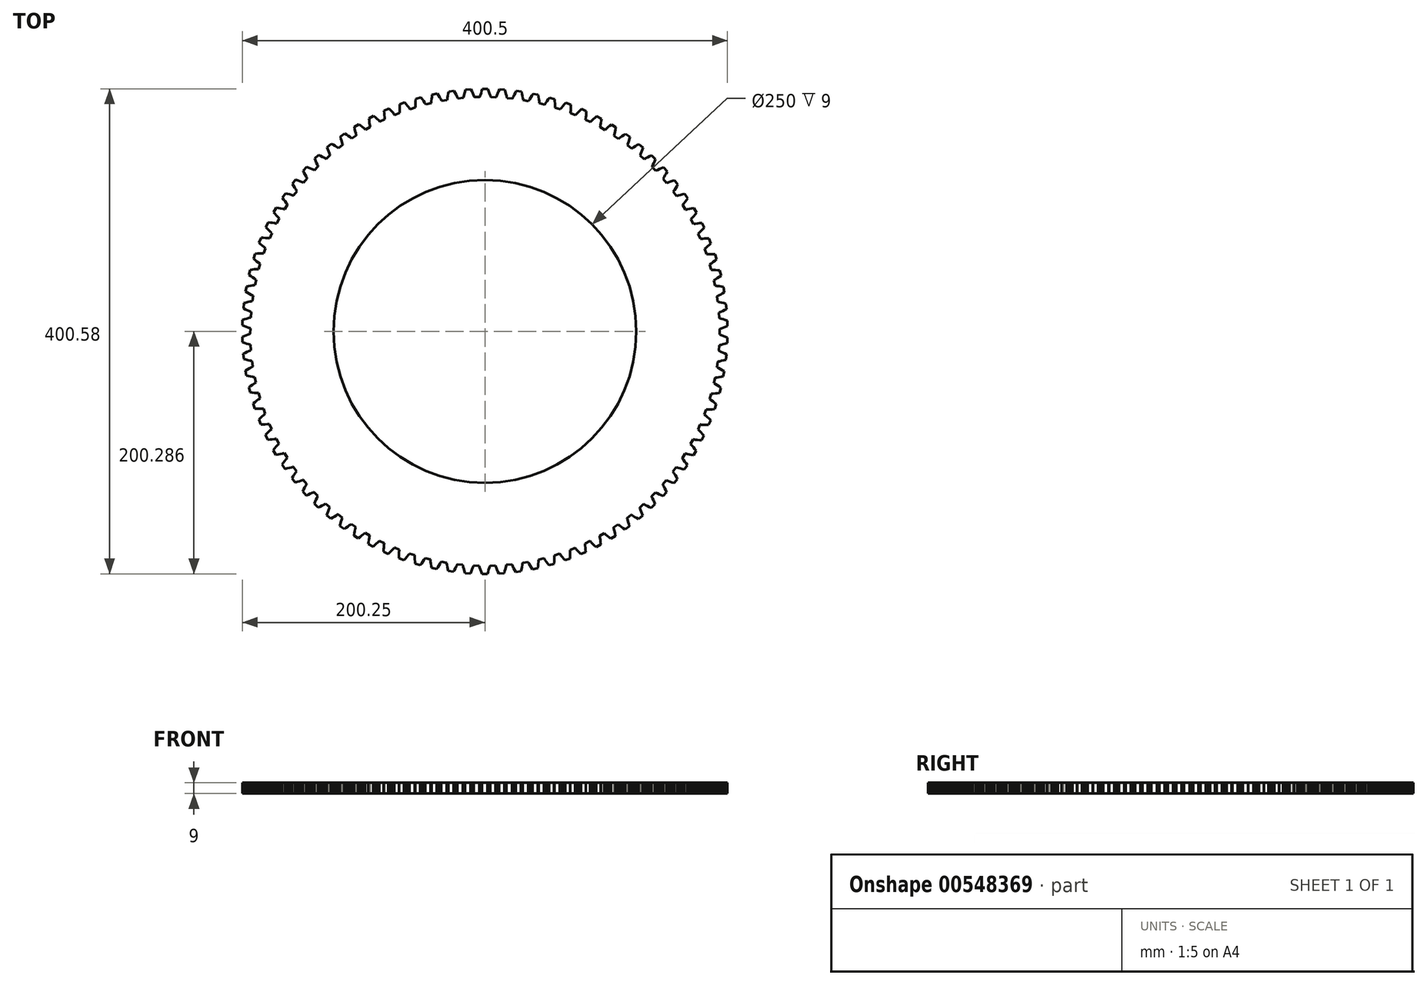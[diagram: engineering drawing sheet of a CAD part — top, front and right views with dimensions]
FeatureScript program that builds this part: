
annotation { "Feature Type Name" : "Feature", "Feature Type Description" : "" }
export const myFeature = defineFeature(function(context is Context, id is Id, definition is map)
    precondition{}
    {
        {
            var Q0;
            Q0=qCreatedBy(makeId("Top.planeOp"),FACE);
            var sketch = newSketch(context, id + "F0", { "sketchPlane" : qUnion([Q0])});
            skLineSegment(sketch, "E0.0.0", {"start": v(83.63, 88.8) * mm, "end": v(83.62, 84.25) * mm});
            skLineSegment(sketch, "E0.0.1", {"start": v(83.62, 84.25) * mm, "end": v(84.03, 84.11) * mm});
            skLineSegment(sketch, "E0.0.2", {"start": v(84.03, 84.11) * mm, "end": v(84.44, 83.97) * mm});
            skLineSegment(sketch, "E0.0.3", {"start": v(84.44, 83.97) * mm, "end": v(85.27, 83.69) * mm});
            skLineSegment(sketch, "E0.0.4", {"start": v(85.27, 83.69) * mm, "end": v(86.9, 83.08) * mm});
            skLineSegment(sketch, "E0.0.5", {"start": v(86.9, 83.08) * mm, "end": v(88.54, 82.43) * mm});
            skLineSegment(sketch, "E0.0.6", {"start": v(88.54, 82.43) * mm, "end": v(90.18, 81.73) * mm});
            skLineSegment(sketch, "E0.0.7", {"start": v(90.18, 81.73) * mm, "end": v(90.02, 77.33) * mm});
            skLineSegment(sketch, "E0.0.8", {"start": v(90.02, 77.33) * mm, "end": v(88.34, 76.75) * mm});
            skLineSegment(sketch, "E0.0.9", {"start": v(88.34, 76.75) * mm, "end": v(86.66, 76.21) * mm});
            skLineSegment(sketch, "E0.0.10", {"start": v(86.66, 76.21) * mm, "end": v(84.98, 75.72) * mm});
            skLineSegment(sketch, "E0.0.11", {"start": v(84.98, 75.72) * mm, "end": v(84.14, 75.5) * mm});
            skLineSegment(sketch, "E0.0.12", {"start": v(84.14, 75.5) * mm, "end": v(83.72, 75.4) * mm});
            skLineSegment(sketch, "E0.0.13", {"start": v(83.72, 75.4) * mm, "end": v(83.3, 75.29) * mm});
            skLineSegment(sketch, "E0.0.14", {"start": v(83.3, 75.29) * mm, "end": v(82.97, 70.74) * mm});
            skLineSegment(sketch, "E0.0.15", {"start": v(82.97, 70.74) * mm, "end": v(83.37, 70.58) * mm});
            skLineSegment(sketch, "E0.0.16", {"start": v(83.37, 70.58) * mm, "end": v(83.77, 70.41) * mm});
            skLineSegment(sketch, "E0.0.17", {"start": v(83.77, 70.41) * mm, "end": v(84.57, 70.07) * mm});
            skLineSegment(sketch, "E0.0.18", {"start": v(84.57, 70.07) * mm, "end": v(86.17, 69.35) * mm});
            skLineSegment(sketch, "E0.0.19", {"start": v(86.17, 69.35) * mm, "end": v(87.75, 68.58) * mm});
            skLineSegment(sketch, "E0.0.20", {"start": v(87.75, 68.58) * mm, "end": v(89.33, 67.77) * mm});
            skLineSegment(sketch, "E0.0.21", {"start": v(89.33, 67.77) * mm, "end": v(88.87, 63.4) * mm});
            skLineSegment(sketch, "E0.0.22", {"start": v(88.87, 63.4) * mm, "end": v(87.15, 62.93) * mm});
            skLineSegment(sketch, "E0.0.23", {"start": v(87.15, 62.93) * mm, "end": v(85.44, 62.51) * mm});
            skLineSegment(sketch, "E0.0.24", {"start": v(85.44, 62.51) * mm, "end": v(83.73, 62.15) * mm});
            skLineSegment(sketch, "E0.0.25", {"start": v(83.73, 62.15) * mm, "end": v(82.88, 61.98) * mm});
            skLineSegment(sketch, "E0.0.26", {"start": v(82.88, 61.98) * mm, "end": v(82.45, 61.9) * mm});
            skLineSegment(sketch, "E0.0.27", {"start": v(82.45, 61.9) * mm, "end": v(82.02, 61.83) * mm});
            skLineSegment(sketch, "E0.0.28", {"start": v(82.02, 61.83) * mm, "end": v(81.38, 57.31) * mm});
            skLineSegment(sketch, "E0.0.29", {"start": v(81.38, 57.31) * mm, "end": v(81.77, 57.12) * mm});
            skLineSegment(sketch, "E0.0.30", {"start": v(81.77, 57.12) * mm, "end": v(82.16, 56.93) * mm});
            skLineSegment(sketch, "E0.0.31", {"start": v(82.16, 56.93) * mm, "end": v(82.93, 56.54) * mm});
            skLineSegment(sketch, "E0.0.32", {"start": v(82.93, 56.54) * mm, "end": v(84.47, 55.7) * mm});
            skLineSegment(sketch, "E0.0.33", {"start": v(84.47, 55.7) * mm, "end": v(86, 54.83) * mm});
            skLineSegment(sketch, "E0.0.34", {"start": v(86, 54.83) * mm, "end": v(87.52, 53.9) * mm});
            skLineSegment(sketch, "E0.0.35", {"start": v(87.52, 53.9) * mm, "end": v(86.75, 49.57) * mm});
            skLineSegment(sketch, "E0.0.36", {"start": v(86.75, 49.57) * mm, "end": v(85, 49.23) * mm});
            skLineSegment(sketch, "E0.0.37", {"start": v(85, 49.23) * mm, "end": v(83.27, 48.94) * mm});
            skLineSegment(sketch, "E0.0.38", {"start": v(83.27, 48.94) * mm, "end": v(81.54, 48.69) * mm});
            skLineSegment(sketch, "E0.0.39", {"start": v(81.54, 48.69) * mm, "end": v(80.68, 48.58) * mm});
            skLineSegment(sketch, "E0.0.40", {"start": v(80.68, 48.58) * mm, "end": v(80.24, 48.53) * mm});
            skLineSegment(sketch, "E0.0.41", {"start": v(80.24, 48.53) * mm, "end": v(79.82, 48.5) * mm});
            skLineSegment(sketch, "E0.0.42", {"start": v(79.82, 48.5) * mm, "end": v(78.86, 44.03) * mm});
            skLineSegment(sketch, "E0.0.43", {"start": v(78.86, 44.03) * mm, "end": v(79.23, 43.82) * mm});
            skLineSegment(sketch, "E0.0.44", {"start": v(79.23, 43.82) * mm, "end": v(79.6, 43.6) * mm});
            skLineSegment(sketch, "E0.0.45", {"start": v(79.6, 43.6) * mm, "end": v(80.35, 43.15) * mm});
            skLineSegment(sketch, "E0.0.46", {"start": v(80.35, 43.15) * mm, "end": v(81.83, 42.21) * mm});
            skLineSegment(sketch, "E0.0.47", {"start": v(81.83, 42.21) * mm, "end": v(83.3, 41.23) * mm});
            skLineSegment(sketch, "E0.0.48", {"start": v(83.3, 41.23) * mm, "end": v(84.75, 40.2) * mm});
            skLineSegment(sketch, "E0.0.49", {"start": v(84.75, 40.2) * mm, "end": v(83.67, 35.93) * mm});
            skLineSegment(sketch, "E0.0.50", {"start": v(83.67, 35.93) * mm, "end": v(81.91, 35.72) * mm});
            skLineSegment(sketch, "E0.0.51", {"start": v(81.91, 35.72) * mm, "end": v(80.16, 35.54) * mm});
            skLineSegment(sketch, "E0.0.52", {"start": v(80.16, 35.54) * mm, "end": v(78.41, 35.42) * mm});
            skLineSegment(sketch, "E0.0.53", {"start": v(78.41, 35.42) * mm, "end": v(77.54, 35.37) * mm});
            skLineSegment(sketch, "E0.0.54", {"start": v(77.54, 35.37) * mm, "end": v(77.11, 35.35) * mm});
            skLineSegment(sketch, "E0.0.55", {"start": v(77.11, 35.35) * mm, "end": v(76.68, 35.34) * mm});
            skLineSegment(sketch, "E0.0.56", {"start": v(76.68, 35.34) * mm, "end": v(75.42, 30.96) * mm});
            skLineSegment(sketch, "E0.0.57", {"start": v(75.42, 30.96) * mm, "end": v(75.78, 30.72) * mm});
            skLineSegment(sketch, "E0.0.58", {"start": v(75.78, 30.72) * mm, "end": v(76.13, 30.47) * mm});
            skLineSegment(sketch, "E0.0.59", {"start": v(76.13, 30.47) * mm, "end": v(76.84, 29.97) * mm});
            skLineSegment(sketch, "E0.0.60", {"start": v(76.84, 29.97) * mm, "end": v(78.25, 28.94) * mm});
            skLineSegment(sketch, "E0.0.61", {"start": v(78.25, 28.94) * mm, "end": v(79.64, 27.85) * mm});
            skLineSegment(sketch, "E0.0.62", {"start": v(79.64, 27.85) * mm, "end": v(81.02, 26.73) * mm});
            skLineSegment(sketch, "E0.0.63", {"start": v(81.02, 26.73) * mm, "end": v(79.65, 22.54) * mm});
            skLineSegment(sketch, "E0.0.64", {"start": v(79.65, 22.54) * mm, "end": v(77.88, 22.45) * mm});
            skLineSegment(sketch, "E0.0.65", {"start": v(77.88, 22.45) * mm, "end": v(76.12, 22.4) * mm});
            skLineSegment(sketch, "E0.0.66", {"start": v(76.12, 22.4) * mm, "end": v(74.37, 22.4) * mm});
            skLineSegment(sketch, "E0.0.67", {"start": v(74.37, 22.4) * mm, "end": v(73.5, 22.4) * mm});
            skLineSegment(sketch, "E0.0.68", {"start": v(73.5, 22.4) * mm, "end": v(73.07, 22.42) * mm});
            skLineSegment(sketch, "E0.0.69", {"start": v(73.07, 22.42) * mm, "end": v(72.64, 22.44) * mm});
            skLineSegment(sketch, "E0.0.70", {"start": v(72.64, 22.44) * mm, "end": v(71.07, 18.16) * mm});
            skLineSegment(sketch, "E0.0.71", {"start": v(71.07, 18.16) * mm, "end": v(71.41, 17.89) * mm});
            skLineSegment(sketch, "E0.0.72", {"start": v(71.41, 17.89) * mm, "end": v(71.75, 17.62) * mm});
            skLineSegment(sketch, "E0.0.73", {"start": v(71.75, 17.62) * mm, "end": v(72.42, 17.07) * mm});
            skLineSegment(sketch, "E0.0.74", {"start": v(72.42, 17.07) * mm, "end": v(73.76, 15.94) * mm});
            skLineSegment(sketch, "E0.0.75", {"start": v(73.76, 15.94) * mm, "end": v(75.07, 14.77) * mm});
            skLineSegment(sketch, "E0.0.76", {"start": v(75.07, 14.77) * mm, "end": v(76.37, 13.55) * mm});
            skLineSegment(sketch, "E0.0.77", {"start": v(76.37, 13.55) * mm, "end": v(74.71, 9.47) * mm});
            skLineSegment(sketch, "E0.0.78", {"start": v(74.71, 9.47) * mm, "end": v(72.93, 9.5) * mm});
            skLineSegment(sketch, "E0.0.79", {"start": v(72.93, 9.5) * mm, "end": v(71.17, 9.57) * mm});
            skLineSegment(sketch, "E0.0.80", {"start": v(71.17, 9.57) * mm, "end": v(69.43, 9.69) * mm});
            skLineSegment(sketch, "E0.0.81", {"start": v(69.43, 9.69) * mm, "end": v(68.56, 9.76) * mm});
            skLineSegment(sketch, "E0.0.82", {"start": v(68.56, 9.76) * mm, "end": v(68.13, 9.8) * mm});
            skLineSegment(sketch, "E0.0.83", {"start": v(68.13, 9.8) * mm, "end": v(67.7, 9.85) * mm});
            skLineSegment(sketch, "E0.0.84", {"start": v(67.7, 9.85) * mm, "end": v(65.84, 5.69) * mm});
            skLineSegment(sketch, "E0.0.85", {"start": v(65.84, 5.69) * mm, "end": v(66.16, 5.4) * mm});
            skLineSegment(sketch, "E0.0.86", {"start": v(66.16, 5.4) * mm, "end": v(66.48, 5.1) * mm});
            skLineSegment(sketch, "E0.0.87", {"start": v(66.48, 5.1) * mm, "end": v(67.12, 4.51) * mm});
            skLineSegment(sketch, "E0.0.88", {"start": v(67.12, 4.51) * mm, "end": v(68.37, 3.3) * mm});
            skLineSegment(sketch, "E0.0.89", {"start": v(68.37, 3.3) * mm, "end": v(69.6, 2.03) * mm});
            skLineSegment(sketch, "E0.0.90", {"start": v(69.6, 2.03) * mm, "end": v(70.8, 0.72) * mm});
            skLineSegment(sketch, "E0.0.91", {"start": v(70.8, 0.72) * mm, "end": v(68.87, -3.23) * mm});
            skLineSegment(sketch, "E0.0.92", {"start": v(68.87, -3.23) * mm, "end": v(67.1, -3.08) * mm});
            skLineSegment(sketch, "E0.0.93", {"start": v(67.1, -3.08) * mm, "end": v(65.34, -2.89) * mm});
            skLineSegment(sketch, "E0.0.94", {"start": v(65.34, -2.89) * mm, "end": v(63.61, -2.65) * mm});
            skLineSegment(sketch, "E0.0.95", {"start": v(63.61, -2.65) * mm, "end": v(62.75, -2.51) * mm});
            skLineSegment(sketch, "E0.0.96", {"start": v(62.75, -2.51) * mm, "end": v(62.33, -2.44) * mm});
            skLineSegment(sketch, "E0.0.97", {"start": v(62.33, -2.44) * mm, "end": v(61.9, -2.36) * mm});
            skLineSegment(sketch, "E0.0.98", {"start": v(61.9, -2.36) * mm, "end": v(59.76, -6.38) * mm});
            skLineSegment(sketch, "E0.0.99", {"start": v(59.76, -6.38) * mm, "end": v(60.06, -6.7) * mm});
            skLineSegment(sketch, "E0.0.100", {"start": v(60.06, -6.7) * mm, "end": v(60.35, -7.01) * mm});
            skLineSegment(sketch, "E0.0.101", {"start": v(60.35, -7.01) * mm, "end": v(60.94, -7.65) * mm});
            skLineSegment(sketch, "E0.0.102", {"start": v(60.94, -7.65) * mm, "end": v(62.1, -8.95) * mm});
            skLineSegment(sketch, "E0.0.103", {"start": v(62.1, -8.95) * mm, "end": v(63.24, -10.3) * mm});
            skLineSegment(sketch, "E0.0.104", {"start": v(63.24, -10.3) * mm, "end": v(64.36, -11.68) * mm});
            skLineSegment(sketch, "E0.0.105", {"start": v(64.36, -11.68) * mm, "end": v(62.15, -15.5) * mm});
            skLineSegment(sketch, "E0.0.106", {"start": v(62.15, -15.5) * mm, "end": v(60.4, -15.22) * mm});
            skLineSegment(sketch, "E0.0.107", {"start": v(60.4, -15.22) * mm, "end": v(58.66, -14.9) * mm});
            skLineSegment(sketch, "E0.0.108", {"start": v(58.66, -14.9) * mm, "end": v(56.95, -14.54) * mm});
            skLineSegment(sketch, "E0.0.109", {"start": v(56.95, -14.54) * mm, "end": v(56.1, -14.35) * mm});
            skLineSegment(sketch, "E0.0.110", {"start": v(56.1, -14.35) * mm, "end": v(55.68, -14.25) * mm});
            skLineSegment(sketch, "E0.0.111", {"start": v(55.68, -14.25) * mm, "end": v(55.26, -14.14) * mm});
            skLineSegment(sketch, "E0.0.112", {"start": v(55.26, -14.14) * mm, "end": v(52.84, -18) * mm});
            skLineSegment(sketch, "E0.0.113", {"start": v(52.84, -18) * mm, "end": v(53.12, -18.34) * mm});
            skLineSegment(sketch, "E0.0.114", {"start": v(53.12, -18.34) * mm, "end": v(53.4, -18.67) * mm});
            skLineSegment(sketch, "E0.0.115", {"start": v(53.4, -18.67) * mm, "end": v(53.94, -19.35) * mm});
            skLineSegment(sketch, "E0.0.116", {"start": v(53.94, -19.35) * mm, "end": v(55, -20.73) * mm});
            skLineSegment(sketch, "E0.0.117", {"start": v(55, -20.73) * mm, "end": v(56.05, -22.15) * mm});
            skLineSegment(sketch, "E0.0.118", {"start": v(56.05, -22.15) * mm, "end": v(57.06, -23.61) * mm});
            skLineSegment(sketch, "E0.0.119", {"start": v(57.06, -23.61) * mm, "end": v(54.6, -27.26) * mm});
            skLineSegment(sketch, "E0.0.120", {"start": v(54.6, -27.26) * mm, "end": v(52.86, -26.86) * mm});
            skLineSegment(sketch, "E0.0.121", {"start": v(52.86, -26.86) * mm, "end": v(51.15, -26.42) * mm});
            skLineSegment(sketch, "E0.0.122", {"start": v(51.15, -26.42) * mm, "end": v(49.47, -25.95) * mm});
            skLineSegment(sketch, "E0.0.123", {"start": v(49.47, -25.95) * mm, "end": v(48.64, -25.7) * mm});
            skLineSegment(sketch, "E0.0.124", {"start": v(48.64, -25.7) * mm, "end": v(48.23, -25.56) * mm});
            skLineSegment(sketch, "E0.0.125", {"start": v(48.23, -25.56) * mm, "end": v(47.82, -25.43) * mm});
            skLineSegment(sketch, "E0.0.126", {"start": v(47.82, -25.43) * mm, "end": v(45.13, -29.11) * mm});
            skLineSegment(sketch, "E0.0.127", {"start": v(45.13, -29.11) * mm, "end": v(45.39, -29.46) * mm});
            skLineSegment(sketch, "E0.0.128", {"start": v(45.39, -29.46) * mm, "end": v(45.64, -29.81) * mm});
            skLineSegment(sketch, "E0.0.129", {"start": v(45.64, -29.81) * mm, "end": v(46.14, -30.53) * mm});
            skLineSegment(sketch, "E0.0.130", {"start": v(46.14, -30.53) * mm, "end": v(47.1, -31.98) * mm});
            skLineSegment(sketch, "E0.0.131", {"start": v(47.1, -31.98) * mm, "end": v(48.04, -33.47) * mm});
            skLineSegment(sketch, "E0.0.132", {"start": v(48.04, -33.47) * mm, "end": v(48.95, -35) * mm});
            skLineSegment(sketch, "E0.0.133", {"start": v(48.95, -35) * mm, "end": v(46.24, -38.47) * mm});
            skLineSegment(sketch, "E0.0.134", {"start": v(46.24, -38.47) * mm, "end": v(44.54, -37.95) * mm});
            skLineSegment(sketch, "E0.0.135", {"start": v(44.54, -37.95) * mm, "end": v(42.86, -37.4) * mm});
            skLineSegment(sketch, "E0.0.136", {"start": v(42.86, -37.4) * mm, "end": v(41.22, -36.8) * mm});
            skLineSegment(sketch, "E0.0.137", {"start": v(41.22, -36.8) * mm, "end": v(40.4, -36.49) * mm});
            skLineSegment(sketch, "E0.0.138", {"start": v(40.4, -36.49) * mm, "end": v(40, -36.33) * mm});
            skLineSegment(sketch, "E0.0.139", {"start": v(40, -36.33) * mm, "end": v(39.6, -36.17) * mm});
            skLineSegment(sketch, "E0.0.140", {"start": v(39.6, -36.17) * mm, "end": v(36.67, -39.66) * mm});
            skLineSegment(sketch, "E0.0.141", {"start": v(36.67, -39.66) * mm, "end": v(36.9, -40.02) * mm});
            skLineSegment(sketch, "E0.0.142", {"start": v(36.9, -40.02) * mm, "end": v(37.13, -40.4) * mm});
            skLineSegment(sketch, "E0.0.143", {"start": v(37.13, -40.4) * mm, "end": v(37.57, -41.14) * mm});
            skLineSegment(sketch, "E0.0.144", {"start": v(37.57, -41.14) * mm, "end": v(38.44, -42.66) * mm});
            skLineSegment(sketch, "E0.0.145", {"start": v(38.44, -42.66) * mm, "end": v(39.27, -44.2) * mm});
            skLineSegment(sketch, "E0.0.146", {"start": v(39.27, -44.2) * mm, "end": v(40.07, -45.8) * mm});
            skLineSegment(sketch, "E0.0.147", {"start": v(40.07, -45.8) * mm, "end": v(37.12, -49.06) * mm});
            skLineSegment(sketch, "E0.0.148", {"start": v(37.12, -49.06) * mm, "end": v(35.46, -48.43) * mm});
            skLineSegment(sketch, "E0.0.149", {"start": v(35.46, -48.43) * mm, "end": v(33.83, -47.76) * mm});
            skLineSegment(sketch, "E0.0.150", {"start": v(33.83, -47.76) * mm, "end": v(32.23, -47.05) * mm});
            skLineSegment(sketch, "E0.0.151", {"start": v(32.23, -47.05) * mm, "end": v(31.44, -46.69) * mm});
            skLineSegment(sketch, "E0.0.152", {"start": v(31.44, -46.69) * mm, "end": v(31.05, -46.5) * mm});
            skLineSegment(sketch, "E0.0.153", {"start": v(31.05, -46.5) * mm, "end": v(30.66, -46.3) * mm});
            skLineSegment(sketch, "E0.0.154", {"start": v(30.66, -46.3) * mm, "end": v(27.5, -49.58) * mm});
            skLineSegment(sketch, "E0.0.155", {"start": v(27.5, -49.58) * mm, "end": v(27.7, -49.96) * mm});
            skLineSegment(sketch, "E0.0.156", {"start": v(27.7, -49.96) * mm, "end": v(27.9, -50.35) * mm});
            skLineSegment(sketch, "E0.0.157", {"start": v(27.9, -50.35) * mm, "end": v(28.29, -51.12) * mm});
            skLineSegment(sketch, "E0.0.158", {"start": v(28.29, -51.12) * mm, "end": v(29.05, -52.7) * mm});
            skLineSegment(sketch, "E0.0.159", {"start": v(29.05, -52.7) * mm, "end": v(29.77, -54.3) * mm});
            skLineSegment(sketch, "E0.0.160", {"start": v(29.77, -54.3) * mm, "end": v(30.46, -55.95) * mm});
            skLineSegment(sketch, "E0.0.161", {"start": v(30.46, -55.95) * mm, "end": v(27.28, -59) * mm});
            skLineSegment(sketch, "E0.0.162", {"start": v(27.28, -59) * mm, "end": v(25.67, -58.25) * mm});
            skLineSegment(sketch, "E0.0.163", {"start": v(25.67, -58.25) * mm, "end": v(24.1, -57.47) * mm});
            skLineSegment(sketch, "E0.0.164", {"start": v(24.1, -57.47) * mm, "end": v(22.55, -56.65) * mm});
            skLineSegment(sketch, "E0.0.165", {"start": v(22.55, -56.65) * mm, "end": v(21.79, -56.23) * mm});
            skLineSegment(sketch, "E0.0.166", {"start": v(21.79, -56.23) * mm, "end": v(21.41, -56.02) * mm});
            skLineSegment(sketch, "E0.0.167", {"start": v(21.41, -56.02) * mm, "end": v(21.04, -55.8) * mm});
            skLineSegment(sketch, "E0.0.168", {"start": v(21.04, -55.8) * mm, "end": v(17.64, -58.85) * mm});
            skLineSegment(sketch, "E0.0.169", {"start": v(17.64, -58.85) * mm, "end": v(17.82, -59.24) * mm});
            skLineSegment(sketch, "E0.0.170", {"start": v(17.82, -59.24) * mm, "end": v(18, -59.64) * mm});
            skLineSegment(sketch, "E0.0.171", {"start": v(18, -59.64) * mm, "end": v(18.33, -60.44) * mm});
            skLineSegment(sketch, "E0.0.172", {"start": v(18.33, -60.44) * mm, "end": v(18.98, -62.06) * mm});
            skLineSegment(sketch, "E0.0.173", {"start": v(18.98, -62.06) * mm, "end": v(19.58, -63.72) * mm});
            skLineSegment(sketch, "E0.0.174", {"start": v(19.58, -63.72) * mm, "end": v(20.16, -65.4) * mm});
            skLineSegment(sketch, "E0.0.175", {"start": v(20.16, -65.4) * mm, "end": v(16.78, -68.23) * mm});
            skLineSegment(sketch, "E0.0.176", {"start": v(16.78, -68.23) * mm, "end": v(15.22, -67.37) * mm});
            skLineSegment(sketch, "E0.0.177", {"start": v(15.22, -67.37) * mm, "end": v(13.7, -66.48) * mm});
            skLineSegment(sketch, "E0.0.178", {"start": v(13.7, -66.48) * mm, "end": v(12.22, -65.55) * mm});
            skLineSegment(sketch, "E0.0.179", {"start": v(12.22, -65.55) * mm, "end": v(11.49, -65.08) * mm});
            skLineSegment(sketch, "E0.0.180", {"start": v(11.49, -65.08) * mm, "end": v(11.13, -64.84) * mm});
            skLineSegment(sketch, "E0.0.181", {"start": v(11.13, -64.84) * mm, "end": v(10.77, -64.6) * mm});
            skLineSegment(sketch, "E0.0.182", {"start": v(10.77, -64.6) * mm, "end": v(7.17, -67.4) * mm});
            skLineSegment(sketch, "E0.0.183", {"start": v(7.17, -67.4) * mm, "end": v(7.32, -67.8) * mm});
            skLineSegment(sketch, "E0.0.184", {"start": v(7.32, -67.8) * mm, "end": v(7.47, -68.21) * mm});
            skLineSegment(sketch, "E0.0.185", {"start": v(7.47, -68.21) * mm, "end": v(7.75, -69.04) * mm});
            skLineSegment(sketch, "E0.0.186", {"start": v(7.75, -69.04) * mm, "end": v(8.28, -70.7) * mm});
            skLineSegment(sketch, "E0.0.187", {"start": v(8.28, -70.7) * mm, "end": v(8.77, -72.4) * mm});
            skLineSegment(sketch, "E0.0.188", {"start": v(8.77, -72.4) * mm, "end": v(9.22, -74.11) * mm});
            skLineSegment(sketch, "E0.0.189", {"start": v(9.22, -74.11) * mm, "end": v(5.66, -76.7) * mm});
            skLineSegment(sketch, "E0.0.190", {"start": v(5.66, -76.7) * mm, "end": v(4.16, -75.73) * mm});
            skLineSegment(sketch, "E0.0.191", {"start": v(4.16, -75.73) * mm, "end": v(2.7, -74.74) * mm});
            skLineSegment(sketch, "E0.0.192", {"start": v(2.7, -74.74) * mm, "end": v(1.3, -73.71) * mm});
            skLineSegment(sketch, "E0.0.193", {"start": v(1.3, -73.71) * mm, "end": v(0.6, -73.19) * mm});
            skLineSegment(sketch, "E0.0.194", {"start": v(0.6, -73.19) * mm, "end": v(0.26, -72.92) * mm});
            skLineSegment(sketch, "E0.0.195", {"start": v(0.26, -72.92) * mm, "end": v(-0.08, -72.66) * mm});
            skLineSegment(sketch, "E0.0.196", {"start": v(-0.08, -72.66) * mm, "end": v(-3.87, -75.2) * mm});
            skLineSegment(sketch, "E0.0.197", {"start": v(-3.87, -75.2) * mm, "end": v(-3.75, -75.62) * mm});
            skLineSegment(sketch, "E0.0.198", {"start": v(-3.75, -75.62) * mm, "end": v(-3.63, -76.03) * mm});
            skLineSegment(sketch, "E0.0.199", {"start": v(-3.63, -76.03) * mm, "end": v(-3.41, -76.87) * mm});
            skLineSegment(sketch, "E0.0.200", {"start": v(-3.41, -76.87) * mm, "end": v(-3, -78.57) * mm});
            skLineSegment(sketch, "E0.0.201", {"start": v(-3, -78.57) * mm, "end": v(-2.62, -80.3) * mm});
            skLineSegment(sketch, "E0.0.202", {"start": v(-2.62, -80.3) * mm, "end": v(-2.3, -82.04) * mm});
            skLineSegment(sketch, "E0.0.203", {"start": v(-2.3, -82.04) * mm, "end": v(-6.03, -84.37) * mm});
            skLineSegment(sketch, "E0.0.204", {"start": v(-6.03, -84.37) * mm, "end": v(-7.45, -83.3) * mm});
            skLineSegment(sketch, "E0.0.205", {"start": v(-7.45, -83.3) * mm, "end": v(-8.83, -82.2) * mm});
            skLineSegment(sketch, "E0.0.206", {"start": v(-8.83, -82.2) * mm, "end": v(-10.18, -81.09) * mm});
            skLineSegment(sketch, "E0.0.207", {"start": v(-10.18, -81.09) * mm, "end": v(-10.83, -80.52) * mm});
            skLineSegment(sketch, "E0.0.208", {"start": v(-10.83, -80.52) * mm, "end": v(-11.15, -80.23) * mm});
            skLineSegment(sketch, "E0.0.209", {"start": v(-11.15, -80.23) * mm, "end": v(-11.48, -79.94) * mm});
            skLineSegment(sketch, "E0.0.210", {"start": v(-11.48, -79.94) * mm, "end": v(-15.43, -82.21) * mm});
            skLineSegment(sketch, "E0.0.211", {"start": v(-15.43, -82.21) * mm, "end": v(-15.34, -82.64) * mm});
            skLineSegment(sketch, "E0.0.212", {"start": v(-15.34, -82.64) * mm, "end": v(-15.25, -83.06) * mm});
            skLineSegment(sketch, "E0.0.213", {"start": v(-15.25, -83.06) * mm, "end": v(-15.09, -83.91) * mm});
            skLineSegment(sketch, "E0.0.214", {"start": v(-15.09, -83.91) * mm, "end": v(-14.8, -85.64) * mm});
            skLineSegment(sketch, "E0.0.215", {"start": v(-14.8, -85.64) * mm, "end": v(-14.54, -87.38) * mm});
            skLineSegment(sketch, "E0.0.216", {"start": v(-14.54, -87.38) * mm, "end": v(-14.33, -89.15) * mm});
            skLineSegment(sketch, "E0.0.217", {"start": v(-14.33, -89.15) * mm, "end": v(-18.22, -91.2) * mm});
            skLineSegment(sketch, "E0.0.218", {"start": v(-18.22, -91.2) * mm, "end": v(-19.57, -90.04) * mm});
            skLineSegment(sketch, "E0.0.219", {"start": v(-19.57, -90.04) * mm, "end": v(-20.87, -88.86) * mm});
            skLineSegment(sketch, "E0.0.220", {"start": v(-20.87, -88.86) * mm, "end": v(-22.13, -87.65) * mm});
            skLineSegment(sketch, "E0.0.221", {"start": v(-22.13, -87.65) * mm, "end": v(-22.74, -87.03) * mm});
            skLineSegment(sketch, "E0.0.222", {"start": v(-22.74, -87.03) * mm, "end": v(-23.05, -86.72) * mm});
            skLineSegment(sketch, "E0.0.223", {"start": v(-23.05, -86.72) * mm, "end": v(-23.35, -86.41) * mm});
            skLineSegment(sketch, "E0.0.224", {"start": v(-23.35, -86.41) * mm, "end": v(-27.45, -88.4) * mm});
            skLineSegment(sketch, "E0.0.225", {"start": v(-27.45, -88.4) * mm, "end": v(-27.39, -88.83) * mm});
            skLineSegment(sketch, "E0.0.226", {"start": v(-27.39, -88.83) * mm, "end": v(-27.33, -89.26) * mm});
            skLineSegment(sketch, "E0.0.227", {"start": v(-27.33, -89.26) * mm, "end": v(-27.23, -90.12) * mm});
            skLineSegment(sketch, "E0.0.228", {"start": v(-27.23, -90.12) * mm, "end": v(-27.05, -91.86) * mm});
            skLineSegment(sketch, "E0.0.229", {"start": v(-27.05, -91.86) * mm, "end": v(-26.92, -93.62) * mm});
            skLineSegment(sketch, "E0.0.230", {"start": v(-26.92, -93.62) * mm, "end": v(-26.84, -95.4) * mm});
            skLineSegment(sketch, "E0.0.231", {"start": v(-26.84, -95.4) * mm, "end": v(-30.86, -97.18) * mm});
            skLineSegment(sketch, "E0.0.232", {"start": v(-30.86, -97.18) * mm, "end": v(-32.12, -95.93) * mm});
            skLineSegment(sketch, "E0.0.233", {"start": v(-32.12, -95.93) * mm, "end": v(-33.34, -94.65) * mm});
            skLineSegment(sketch, "E0.0.234", {"start": v(-33.34, -94.65) * mm, "end": v(-34.51, -93.36) * mm});
            skLineSegment(sketch, "E0.0.235", {"start": v(-34.51, -93.36) * mm, "end": v(-35.08, -92.7) * mm});
            skLineSegment(sketch, "E0.0.236", {"start": v(-35.08, -92.7) * mm, "end": v(-35.36, -92.37) * mm});
            skLineSegment(sketch, "E0.0.237", {"start": v(-35.36, -92.37) * mm, "end": v(-35.64, -92.04) * mm});
            skLineSegment(sketch, "E0.0.238", {"start": v(-35.64, -92.04) * mm, "end": v(-39.87, -93.74) * mm});
            skLineSegment(sketch, "E0.0.239", {"start": v(-39.87, -93.74) * mm, "end": v(-39.84, -94.17) * mm});
            skLineSegment(sketch, "E0.0.240", {"start": v(-39.84, -94.17) * mm, "end": v(-39.81, -94.6) * mm});
            skLineSegment(sketch, "E0.0.241", {"start": v(-39.81, -94.6) * mm, "end": v(-39.77, -95.47) * mm});
            skLineSegment(sketch, "E0.0.242", {"start": v(-39.77, -95.47) * mm, "end": v(-39.72, -97.22) * mm});
            skLineSegment(sketch, "E0.0.243", {"start": v(-39.72, -97.22) * mm, "end": v(-39.71, -98.98) * mm});
            skLineSegment(sketch, "E0.0.244", {"start": v(-39.71, -98.98) * mm, "end": v(-39.75, -100.76) * mm});
            skLineSegment(sketch, "E0.0.245", {"start": v(-39.75, -100.76) * mm, "end": v(-43.9, -102.26) * mm});
            skLineSegment(sketch, "E0.0.246", {"start": v(-43.9, -102.26) * mm, "end": v(-45.06, -100.92) * mm});
            skLineSegment(sketch, "E0.0.247", {"start": v(-45.06, -100.92) * mm, "end": v(-46.18, -99.56) * mm});
            skLineSegment(sketch, "E0.0.248", {"start": v(-46.18, -99.56) * mm, "end": v(-47.26, -98.19) * mm});
            skLineSegment(sketch, "E0.0.249", {"start": v(-47.26, -98.19) * mm, "end": v(-47.79, -97.5) * mm});
            skLineSegment(sketch, "E0.0.250", {"start": v(-47.79, -97.5) * mm, "end": v(-48.04, -97.14) * mm});
            skLineSegment(sketch, "E0.0.251", {"start": v(-48.04, -97.14) * mm, "end": v(-48.3, -96.8) * mm});
            skLineSegment(sketch, "E0.0.252", {"start": v(-48.3, -96.8) * mm, "end": v(-52.63, -98.2) * mm});
            skLineSegment(sketch, "E0.0.253", {"start": v(-52.63, -98.2) * mm, "end": v(-52.63, -98.63) * mm});
            skLineSegment(sketch, "E0.0.254", {"start": v(-52.63, -98.63) * mm, "end": v(-52.64, -99.06) * mm});
            skLineSegment(sketch, "E0.0.255", {"start": v(-52.64, -99.06) * mm, "end": v(-52.66, -99.93) * mm});
            skLineSegment(sketch, "E0.0.256", {"start": v(-52.66, -99.93) * mm, "end": v(-52.73, -101.68) * mm});
            skLineSegment(sketch, "E0.0.257", {"start": v(-52.73, -101.68) * mm, "end": v(-52.84, -103.44) * mm});
            skLineSegment(sketch, "E0.0.258", {"start": v(-52.84, -103.44) * mm, "end": v(-53, -105.2) * mm});
            skLineSegment(sketch, "E0.0.259", {"start": v(-53, -105.2) * mm, "end": v(-57.24, -106.41) * mm});
            skLineSegment(sketch, "E0.0.260", {"start": v(-57.24, -106.41) * mm, "end": v(-58.31, -105) * mm});
            skLineSegment(sketch, "E0.0.261", {"start": v(-58.31, -105) * mm, "end": v(-59.34, -103.56) * mm});
            skLineSegment(sketch, "E0.0.262", {"start": v(-59.34, -103.56) * mm, "end": v(-60.32, -102.12) * mm});
            skLineSegment(sketch, "E0.0.263", {"start": v(-60.32, -102.12) * mm, "end": v(-60.8, -101.39) * mm});
            skLineSegment(sketch, "E0.0.264", {"start": v(-60.8, -101.39) * mm, "end": v(-61.02, -101.02) * mm});
            skLineSegment(sketch, "E0.0.265", {"start": v(-61.02, -101.02) * mm, "end": v(-61.25, -100.66) * mm});
            skLineSegment(sketch, "E0.0.266", {"start": v(-61.25, -100.66) * mm, "end": v(-65.68, -101.75) * mm});
            skLineSegment(sketch, "E0.0.267", {"start": v(-65.68, -101.75) * mm, "end": v(-65.7, -102.18) * mm});
            skLineSegment(sketch, "E0.0.268", {"start": v(-65.7, -102.18) * mm, "end": v(-65.74, -102.61) * mm});
            skLineSegment(sketch, "E0.0.269", {"start": v(-65.74, -102.61) * mm, "end": v(-65.82, -103.48) * mm});
            skLineSegment(sketch, "E0.0.270", {"start": v(-65.82, -103.48) * mm, "end": v(-66.01, -105.22) * mm});
            skLineSegment(sketch, "E0.0.271", {"start": v(-66.01, -105.22) * mm, "end": v(-66.25, -106.96) * mm});
            skLineSegment(sketch, "E0.0.272", {"start": v(-66.25, -106.96) * mm, "end": v(-66.54, -108.72) * mm});
            skLineSegment(sketch, "E0.0.273", {"start": v(-66.54, -108.72) * mm, "end": v(-70.85, -109.63) * mm});
            skLineSegment(sketch, "E0.0.274", {"start": v(-70.85, -109.63) * mm, "end": v(-71.82, -108.14) * mm});
            skLineSegment(sketch, "E0.0.275", {"start": v(-71.82, -108.14) * mm, "end": v(-72.74, -106.64) * mm});
            skLineSegment(sketch, "E0.0.276", {"start": v(-72.74, -106.64) * mm, "end": v(-73.62, -105.13) * mm});
            skLineSegment(sketch, "E0.0.277", {"start": v(-73.62, -105.13) * mm, "end": v(-74.04, -104.37) * mm});
            skLineSegment(sketch, "E0.0.278", {"start": v(-74.04, -104.37) * mm, "end": v(-74.25, -103.98) * mm});
            skLineSegment(sketch, "E0.0.279", {"start": v(-74.25, -103.98) * mm, "end": v(-74.45, -103.6) * mm});
            skLineSegment(sketch, "E0.0.280", {"start": v(-74.45, -103.6) * mm, "end": v(-78.94, -104.39) * mm});
            skLineSegment(sketch, "E0.0.281", {"start": v(-78.94, -104.39) * mm, "end": v(-79, -104.82) * mm});
            skLineSegment(sketch, "E0.0.282", {"start": v(-79, -104.82) * mm, "end": v(-79.06, -105.24) * mm});
            skLineSegment(sketch, "E0.0.283", {"start": v(-79.06, -105.24) * mm, "end": v(-79.2, -106.1) * mm});
            skLineSegment(sketch, "E0.0.284", {"start": v(-79.2, -106.1) * mm, "end": v(-79.51, -107.82) * mm});
            skLineSegment(sketch, "E0.0.285", {"start": v(-79.51, -107.82) * mm, "end": v(-79.88, -109.55) * mm});
            skLineSegment(sketch, "E0.0.286", {"start": v(-79.88, -109.55) * mm, "end": v(-80.28, -111.28) * mm});
            skLineSegment(sketch, "E0.0.287", {"start": v(-80.28, -111.28) * mm, "end": v(-84.64, -111.88) * mm});
            skLineSegment(sketch, "E0.0.288", {"start": v(-84.64, -111.88) * mm, "end": v(-85.5, -110.33) * mm});
            skLineSegment(sketch, "E0.0.289", {"start": v(-85.5, -110.33) * mm, "end": v(-86.32, -108.77) * mm});
            skLineSegment(sketch, "E0.0.290", {"start": v(-86.32, -108.77) * mm, "end": v(-87.1, -107.2) * mm});
            skLineSegment(sketch, "E0.0.291", {"start": v(-87.1, -107.2) * mm, "end": v(-87.46, -106.41) * mm});
            skLineSegment(sketch, "E0.0.292", {"start": v(-87.46, -106.41) * mm, "end": v(-87.64, -106.02) * mm});
            skLineSegment(sketch, "E0.0.293", {"start": v(-87.64, -106.02) * mm, "end": v(-87.82, -105.62) * mm});
            skLineSegment(sketch, "E0.0.294", {"start": v(-87.82, -105.62) * mm, "end": v(-92.35, -106.1) * mm});
            skLineSegment(sketch, "E0.0.295", {"start": v(-92.35, -106.1) * mm, "end": v(-92.44, -106.52) * mm});
            skLineSegment(sketch, "E0.0.296", {"start": v(-92.44, -106.52) * mm, "end": v(-92.53, -106.94) * mm});
            skLineSegment(sketch, "E0.0.297", {"start": v(-92.53, -106.94) * mm, "end": v(-92.73, -107.78) * mm});
            skLineSegment(sketch, "E0.0.298", {"start": v(-92.73, -107.78) * mm, "end": v(-93.16, -109.48) * mm});
            skLineSegment(sketch, "E0.0.299", {"start": v(-93.16, -109.48) * mm, "end": v(-93.64, -111.17) * mm});
            skLineSegment(sketch, "E0.0.300", {"start": v(-93.64, -111.17) * mm, "end": v(-94.17, -112.87) * mm});
            skLineSegment(sketch, "E0.0.301", {"start": v(-94.17, -112.87) * mm, "end": v(-98.56, -113.17) * mm});
            skLineSegment(sketch, "E0.0.302", {"start": v(-98.56, -113.17) * mm, "end": v(-99.32, -111.56) * mm});
            skLineSegment(sketch, "E0.0.303", {"start": v(-99.32, -111.56) * mm, "end": v(-100.02, -109.95) * mm});
            skLineSegment(sketch, "E0.0.304", {"start": v(-100.02, -109.95) * mm, "end": v(-100.68, -108.33) * mm});
            skLineSegment(sketch, "E0.0.305", {"start": v(-100.68, -108.33) * mm, "end": v(-101, -107.52) * mm});
            skLineSegment(sketch, "E0.0.306", {"start": v(-101, -107.52) * mm, "end": v(-101.15, -107.11) * mm});
            skLineSegment(sketch, "E0.0.307", {"start": v(-101.15, -107.11) * mm, "end": v(-101.3, -106.7) * mm});
            skLineSegment(sketch, "E0.0.308", {"start": v(-101.3, -106.7) * mm, "end": v(-105.85, -106.86) * mm});
            skLineSegment(sketch, "E0.0.309", {"start": v(-105.85, -106.86) * mm, "end": v(-105.97, -107.27) * mm});
            skLineSegment(sketch, "E0.0.310", {"start": v(-105.97, -107.27) * mm, "end": v(-106.1, -107.69) * mm});
            skLineSegment(sketch, "E0.0.311", {"start": v(-106.1, -107.69) * mm, "end": v(-106.35, -108.52) * mm});
            skLineSegment(sketch, "E0.0.312", {"start": v(-106.35, -108.52) * mm, "end": v(-106.9, -110.18) * mm});
            skLineSegment(sketch, "E0.0.313", {"start": v(-106.9, -110.18) * mm, "end": v(-107.5, -111.84) * mm});
            skLineSegment(sketch, "E0.0.314", {"start": v(-107.5, -111.84) * mm, "end": v(-108.14, -113.5) * mm});
            skLineSegment(sketch, "E0.0.315", {"start": v(-108.14, -113.5) * mm, "end": v(-112.54, -113.49) * mm});
            skLineSegment(sketch, "E0.0.316", {"start": v(-112.54, -113.49) * mm, "end": v(-113.18, -111.83) * mm});
            skLineSegment(sketch, "E0.0.317", {"start": v(-113.18, -111.83) * mm, "end": v(-113.77, -110.17) * mm});
            skLineSegment(sketch, "E0.0.318", {"start": v(-113.77, -110.17) * mm, "end": v(-114.32, -108.5) * mm});
            skLineSegment(sketch, "E0.0.319", {"start": v(-114.32, -108.5) * mm, "end": v(-114.57, -107.68) * mm});
            skLineSegment(sketch, "E0.0.320", {"start": v(-114.57, -107.68) * mm, "end": v(-114.7, -107.26) * mm});
            skLineSegment(sketch, "E0.0.321", {"start": v(-114.7, -107.26) * mm, "end": v(-114.81, -106.85) * mm});
            skLineSegment(sketch, "E0.0.322", {"start": v(-114.81, -106.85) * mm, "end": v(-119.37, -106.68) * mm});
            skLineSegment(sketch, "E0.0.323", {"start": v(-119.37, -106.68) * mm, "end": v(-119.52, -107.09) * mm});
            skLineSegment(sketch, "E0.0.324", {"start": v(-119.52, -107.09) * mm, "end": v(-119.67, -107.5) * mm});
            skLineSegment(sketch, "E0.0.325", {"start": v(-119.67, -107.5) * mm, "end": v(-119.98, -108.3) * mm});
            skLineSegment(sketch, "E0.0.326", {"start": v(-119.98, -108.3) * mm, "end": v(-120.64, -109.92) * mm});
            skLineSegment(sketch, "E0.0.327", {"start": v(-120.64, -109.92) * mm, "end": v(-121.36, -111.53) * mm});
            skLineSegment(sketch, "E0.0.328", {"start": v(-121.36, -111.53) * mm, "end": v(-122.11, -113.14) * mm});
            skLineSegment(sketch, "E0.0.329", {"start": v(-122.11, -113.14) * mm, "end": v(-126.5, -112.83) * mm});
            skLineSegment(sketch, "E0.0.330", {"start": v(-126.5, -112.83) * mm, "end": v(-127.03, -111.13) * mm});
            skLineSegment(sketch, "E0.0.331", {"start": v(-127.03, -111.13) * mm, "end": v(-127.5, -109.43) * mm});
            skLineSegment(sketch, "E0.0.332", {"start": v(-127.5, -109.43) * mm, "end": v(-127.93, -107.74) * mm});
            skLineSegment(sketch, "E0.0.333", {"start": v(-127.93, -107.74) * mm, "end": v(-128.13, -106.89) * mm});
            skLineSegment(sketch, "E0.0.334", {"start": v(-128.13, -106.89) * mm, "end": v(-128.22, -106.47) * mm});
            skLineSegment(sketch, "E0.0.335", {"start": v(-128.22, -106.47) * mm, "end": v(-128.3, -106.04) * mm});
            skLineSegment(sketch, "E0.0.336", {"start": v(-128.3, -106.04) * mm, "end": v(-132.84, -105.56) * mm});
            skLineSegment(sketch, "E0.0.337", {"start": v(-132.84, -105.56) * mm, "end": v(-133.02, -105.96) * mm});
            skLineSegment(sketch, "E0.0.338", {"start": v(-133.02, -105.96) * mm, "end": v(-133.2, -106.35) * mm});
            skLineSegment(sketch, "E0.0.339", {"start": v(-133.2, -106.35) * mm, "end": v(-133.57, -107.14) * mm});
            skLineSegment(sketch, "E0.0.340", {"start": v(-133.57, -107.14) * mm, "end": v(-134.34, -108.7) * mm});
            skLineSegment(sketch, "E0.0.341", {"start": v(-134.34, -108.7) * mm, "end": v(-135.16, -110.26) * mm});
            skLineSegment(sketch, "E0.0.342", {"start": v(-135.16, -110.26) * mm, "end": v(-136.03, -111.81) * mm});
            skLineSegment(sketch, "E0.0.343", {"start": v(-136.03, -111.81) * mm, "end": v(-140.4, -111.2) * mm});
            skLineSegment(sketch, "E0.0.344", {"start": v(-140.4, -111.2) * mm, "end": v(-140.8, -109.46) * mm});
            skLineSegment(sketch, "E0.0.345", {"start": v(-140.8, -109.46) * mm, "end": v(-141.15, -107.74) * mm});
            skLineSegment(sketch, "E0.0.346", {"start": v(-141.15, -107.74) * mm, "end": v(-141.46, -106.02) * mm});
            skLineSegment(sketch, "E0.0.347", {"start": v(-141.46, -106.02) * mm, "end": v(-141.6, -105.16) * mm});
            skLineSegment(sketch, "E0.0.348", {"start": v(-141.6, -105.16) * mm, "end": v(-141.66, -104.73) * mm});
            skLineSegment(sketch, "E0.0.349", {"start": v(-141.66, -104.73) * mm, "end": v(-141.72, -104.3) * mm});
            skLineSegment(sketch, "E0.0.350", {"start": v(-141.72, -104.3) * mm, "end": v(-146.2, -103.5) * mm});
            skLineSegment(sketch, "E0.0.351", {"start": v(-146.2, -103.5) * mm, "end": v(-146.4, -103.88) * mm});
            skLineSegment(sketch, "E0.0.352", {"start": v(-146.4, -103.88) * mm, "end": v(-146.61, -104.26) * mm});
            skLineSegment(sketch, "E0.0.353", {"start": v(-146.61, -104.26) * mm, "end": v(-147.04, -105.02) * mm});
            skLineSegment(sketch, "E0.0.354", {"start": v(-147.04, -105.02) * mm, "end": v(-147.92, -106.53) * mm});
            skLineSegment(sketch, "E0.0.355", {"start": v(-147.92, -106.53) * mm, "end": v(-148.85, -108.03) * mm});
            skLineSegment(sketch, "E0.0.356", {"start": v(-148.85, -108.03) * mm, "end": v(-149.82, -109.52) * mm});
            skLineSegment(sketch, "E0.0.357", {"start": v(-149.82, -109.52) * mm, "end": v(-154.13, -108.6) * mm});
            skLineSegment(sketch, "E0.0.358", {"start": v(-154.13, -108.6) * mm, "end": v(-154.4, -106.84) * mm});
            skLineSegment(sketch, "E0.0.359", {"start": v(-154.4, -106.84) * mm, "end": v(-154.64, -105.1) * mm});
            skLineSegment(sketch, "E0.0.360", {"start": v(-154.64, -105.1) * mm, "end": v(-154.83, -103.36) * mm});
            skLineSegment(sketch, "E0.0.361", {"start": v(-154.83, -103.36) * mm, "end": v(-154.9, -102.49) * mm});
            skLineSegment(sketch, "E0.0.362", {"start": v(-154.9, -102.49) * mm, "end": v(-154.94, -102.06) * mm});
            skLineSegment(sketch, "E0.0.363", {"start": v(-154.94, -102.06) * mm, "end": v(-154.97, -101.63) * mm});
            skLineSegment(sketch, "E0.0.364", {"start": v(-154.97, -101.63) * mm, "end": v(-159.4, -100.52) * mm});
            skLineSegment(sketch, "E0.0.365", {"start": v(-159.4, -100.52) * mm, "end": v(-159.62, -100.88) * mm});
            skLineSegment(sketch, "E0.0.366", {"start": v(-159.62, -100.88) * mm, "end": v(-159.85, -101.25) * mm});
            skLineSegment(sketch, "E0.0.367", {"start": v(-159.85, -101.25) * mm, "end": v(-160.33, -101.98) * mm});
            skLineSegment(sketch, "E0.0.368", {"start": v(-160.33, -101.98) * mm, "end": v(-161.31, -103.42) * mm});
            skLineSegment(sketch, "E0.0.369", {"start": v(-161.31, -103.42) * mm, "end": v(-162.34, -104.85) * mm});
            skLineSegment(sketch, "E0.0.370", {"start": v(-162.34, -104.85) * mm, "end": v(-163.42, -106.27) * mm});
            skLineSegment(sketch, "E0.0.371", {"start": v(-163.42, -106.27) * mm, "end": v(-167.65, -105.05) * mm});
            skLineSegment(sketch, "E0.0.372", {"start": v(-167.65, -105.05) * mm, "end": v(-167.8, -103.28) * mm});
            skLineSegment(sketch, "E0.0.373", {"start": v(-167.8, -103.28) * mm, "end": v(-167.92, -101.52) * mm});
            skLineSegment(sketch, "E0.0.374", {"start": v(-167.92, -101.52) * mm, "end": v(-167.99, -99.77) * mm});
            skLineSegment(sketch, "E0.0.375", {"start": v(-167.99, -99.77) * mm, "end": v(-168, -98.9) * mm});
            skLineSegment(sketch, "E0.0.376", {"start": v(-168, -98.9) * mm, "end": v(-168, -98.47) * mm});
            skLineSegment(sketch, "E0.0.377", {"start": v(-168, -98.47) * mm, "end": v(-168, -98.04) * mm});
            skLineSegment(sketch, "E0.0.378", {"start": v(-168, -98.04) * mm, "end": v(-172.34, -96.62) * mm});
            skLineSegment(sketch, "E0.0.379", {"start": v(-172.34, -96.62) * mm, "end": v(-172.6, -96.97) * mm});
            skLineSegment(sketch, "E0.0.380", {"start": v(-172.6, -96.97) * mm, "end": v(-172.85, -97.32) * mm});
            skLineSegment(sketch, "E0.0.381", {"start": v(-172.85, -97.32) * mm, "end": v(-173.37, -98.01) * mm});
            skLineSegment(sketch, "E0.0.382", {"start": v(-173.37, -98.01) * mm, "end": v(-174.46, -99.38) * mm});
            skLineSegment(sketch, "E0.0.383", {"start": v(-174.46, -99.38) * mm, "end": v(-175.59, -100.74) * mm});
            skLineSegment(sketch, "E0.0.384", {"start": v(-175.59, -100.74) * mm, "end": v(-176.76, -102.07) * mm});
            skLineSegment(sketch, "E0.0.385", {"start": v(-176.76, -102.07) * mm, "end": v(-180.9, -100.56) * mm});
            skLineSegment(sketch, "E0.0.386", {"start": v(-180.9, -100.56) * mm, "end": v(-180.93, -98.78) * mm});
            skLineSegment(sketch, "E0.0.387", {"start": v(-180.93, -98.78) * mm, "end": v(-180.92, -97.02) * mm});
            skLineSegment(sketch, "E0.0.388", {"start": v(-180.92, -97.02) * mm, "end": v(-180.86, -95.27) * mm});
            skLineSegment(sketch, "E0.0.389", {"start": v(-180.86, -95.27) * mm, "end": v(-180.81, -94.4) * mm});
            skLineSegment(sketch, "E0.0.390", {"start": v(-180.81, -94.4) * mm, "end": v(-180.79, -93.97) * mm});
            skLineSegment(sketch, "E0.0.391", {"start": v(-180.79, -93.97) * mm, "end": v(-180.75, -93.54) * mm});
            skLineSegment(sketch, "E0.0.392", {"start": v(-180.75, -93.54) * mm, "end": v(-184.98, -91.83) * mm});
            skLineSegment(sketch, "E0.0.393", {"start": v(-184.98, -91.83) * mm, "end": v(-185.26, -92.16) * mm});
            skLineSegment(sketch, "E0.0.394", {"start": v(-185.26, -92.16) * mm, "end": v(-185.54, -92.49) * mm});
            skLineSegment(sketch, "E0.0.395", {"start": v(-185.54, -92.49) * mm, "end": v(-186.11, -93.14) * mm});
            skLineSegment(sketch, "E0.0.396", {"start": v(-186.11, -93.14) * mm, "end": v(-187.29, -94.44) * mm});
            skLineSegment(sketch, "E0.0.397", {"start": v(-187.29, -94.44) * mm, "end": v(-188.5, -95.7) * mm});
            skLineSegment(sketch, "E0.0.398", {"start": v(-188.5, -95.7) * mm, "end": v(-189.77, -96.96) * mm});
            skLineSegment(sketch, "E0.0.399", {"start": v(-189.77, -96.96) * mm, "end": v(-193.79, -95.16) * mm});
            skLineSegment(sketch, "E0.0.400", {"start": v(-193.79, -95.16) * mm, "end": v(-193.7, -93.39) * mm});
            skLineSegment(sketch, "E0.0.401", {"start": v(-193.7, -93.39) * mm, "end": v(-193.57, -91.63) * mm});
            skLineSegment(sketch, "E0.0.402", {"start": v(-193.57, -91.63) * mm, "end": v(-193.39, -89.9) * mm});
            skLineSegment(sketch, "E0.0.403", {"start": v(-193.39, -89.9) * mm, "end": v(-193.28, -89.03) * mm});
            skLineSegment(sketch, "E0.0.404", {"start": v(-193.28, -89.03) * mm, "end": v(-193.22, -88.6) * mm});
            skLineSegment(sketch, "E0.0.405", {"start": v(-193.22, -88.6) * mm, "end": v(-193.16, -88.17) * mm});
            skLineSegment(sketch, "E0.0.406", {"start": v(-193.16, -88.17) * mm, "end": v(-197.26, -86.17) * mm});
            skLineSegment(sketch, "E0.0.407", {"start": v(-197.26, -86.17) * mm, "end": v(-197.56, -86.48) * mm});
            skLineSegment(sketch, "E0.0.408", {"start": v(-197.56, -86.48) * mm, "end": v(-197.86, -86.79) * mm});
            skLineSegment(sketch, "E0.0.409", {"start": v(-197.86, -86.79) * mm, "end": v(-198.48, -87.4) * mm});
            skLineSegment(sketch, "E0.0.410", {"start": v(-198.48, -87.4) * mm, "end": v(-199.74, -88.6) * mm});
            skLineSegment(sketch, "E0.0.411", {"start": v(-199.74, -88.6) * mm, "end": v(-201.05, -89.8) * mm});
            skLineSegment(sketch, "E0.0.412", {"start": v(-201.05, -89.8) * mm, "end": v(-202.4, -90.95) * mm});
            skLineSegment(sketch, "E0.0.413", {"start": v(-202.4, -90.95) * mm, "end": v(-206.28, -88.88) * mm});
            skLineSegment(sketch, "E0.0.414", {"start": v(-206.28, -88.88) * mm, "end": v(-206.06, -87.12) * mm});
            skLineSegment(sketch, "E0.0.415", {"start": v(-206.06, -87.12) * mm, "end": v(-205.8, -85.37) * mm});
            skLineSegment(sketch, "E0.0.416", {"start": v(-205.8, -85.37) * mm, "end": v(-205.5, -83.65) * mm});
            skLineSegment(sketch, "E0.0.417", {"start": v(-205.5, -83.65) * mm, "end": v(-205.34, -82.8) * mm});
            skLineSegment(sketch, "E0.0.418", {"start": v(-205.34, -82.8) * mm, "end": v(-205.26, -82.37) * mm});
            skLineSegment(sketch, "E0.0.419", {"start": v(-205.26, -82.37) * mm, "end": v(-205.17, -81.95) * mm});
            skLineSegment(sketch, "E0.0.420", {"start": v(-205.17, -81.95) * mm, "end": v(-209.11, -79.66) * mm});
            skLineSegment(sketch, "E0.0.421", {"start": v(-209.11, -79.66) * mm, "end": v(-209.43, -79.95) * mm});
            skLineSegment(sketch, "E0.0.422", {"start": v(-209.43, -79.95) * mm, "end": v(-209.76, -80.24) * mm});
            skLineSegment(sketch, "E0.0.423", {"start": v(-209.76, -80.24) * mm, "end": v(-210.41, -80.8) * mm});
            skLineSegment(sketch, "E0.0.424", {"start": v(-210.41, -80.8) * mm, "end": v(-211.76, -81.92) * mm});
            skLineSegment(sketch, "E0.0.425", {"start": v(-211.76, -81.92) * mm, "end": v(-213.14, -83.01) * mm});
            skLineSegment(sketch, "E0.0.426", {"start": v(-213.14, -83.01) * mm, "end": v(-214.57, -84.08) * mm});
            skLineSegment(sketch, "E0.0.427", {"start": v(-214.57, -84.08) * mm, "end": v(-218.3, -81.74) * mm});
            skLineSegment(sketch, "E0.0.428", {"start": v(-218.3, -81.74) * mm, "end": v(-217.96, -80) * mm});
            skLineSegment(sketch, "E0.0.429", {"start": v(-217.96, -80) * mm, "end": v(-217.58, -78.27) * mm});
            skLineSegment(sketch, "E0.0.430", {"start": v(-217.58, -78.27) * mm, "end": v(-217.17, -76.58) * mm});
            skLineSegment(sketch, "E0.0.431", {"start": v(-217.17, -76.58) * mm, "end": v(-216.94, -75.74) * mm});
            skLineSegment(sketch, "E0.0.432", {"start": v(-216.94, -75.74) * mm, "end": v(-216.82, -75.32) * mm});
            skLineSegment(sketch, "E0.0.433", {"start": v(-216.82, -75.32) * mm, "end": v(-216.7, -74.9) * mm});
            skLineSegment(sketch, "E0.0.434", {"start": v(-216.7, -74.9) * mm, "end": v(-220.48, -72.35) * mm});
            skLineSegment(sketch, "E0.0.435", {"start": v(-220.48, -72.35) * mm, "end": v(-220.82, -72.62) * mm});
            skLineSegment(sketch, "E0.0.436", {"start": v(-220.82, -72.62) * mm, "end": v(-221.16, -72.88) * mm});
            skLineSegment(sketch, "E0.0.437", {"start": v(-221.16, -72.88) * mm, "end": v(-221.86, -73.4) * mm});
            skLineSegment(sketch, "E0.0.438", {"start": v(-221.86, -73.4) * mm, "end": v(-223.28, -74.42) * mm});
            skLineSegment(sketch, "E0.0.439", {"start": v(-223.28, -74.42) * mm, "end": v(-224.74, -75.41) * mm});
            skLineSegment(sketch, "E0.0.440", {"start": v(-224.74, -75.41) * mm, "end": v(-226.23, -76.37) * mm});
            skLineSegment(sketch, "E0.0.441", {"start": v(-226.23, -76.37) * mm, "end": v(-229.8, -73.78) * mm});
            skLineSegment(sketch, "E0.0.442", {"start": v(-229.8, -73.78) * mm, "end": v(-229.33, -72.06) * mm});
            skLineSegment(sketch, "E0.0.443", {"start": v(-229.33, -72.06) * mm, "end": v(-228.84, -70.37) * mm});
            skLineSegment(sketch, "E0.0.444", {"start": v(-228.84, -70.37) * mm, "end": v(-228.3, -68.7) * mm});
            skLineSegment(sketch, "E0.0.445", {"start": v(-228.3, -68.7) * mm, "end": v(-228.02, -67.88) * mm});
            skLineSegment(sketch, "E0.0.446", {"start": v(-228.02, -67.88) * mm, "end": v(-227.87, -67.48) * mm});
            skLineSegment(sketch, "E0.0.447", {"start": v(-227.87, -67.48) * mm, "end": v(-227.72, -67.07) * mm});
            skLineSegment(sketch, "E0.0.448", {"start": v(-227.72, -67.07) * mm, "end": v(-231.31, -64.26) * mm});
            skLineSegment(sketch, "E0.0.449", {"start": v(-231.31, -64.26) * mm, "end": v(-231.67, -64.5) * mm});
            skLineSegment(sketch, "E0.0.450", {"start": v(-231.67, -64.5) * mm, "end": v(-232.03, -64.74) * mm});
            skLineSegment(sketch, "E0.0.451", {"start": v(-232.03, -64.74) * mm, "end": v(-232.76, -65.21) * mm});
            skLineSegment(sketch, "E0.0.452", {"start": v(-232.76, -65.21) * mm, "end": v(-234.25, -66.13) * mm});
            skLineSegment(sketch, "E0.0.453", {"start": v(-234.25, -66.13) * mm, "end": v(-235.77, -67.02) * mm});
            skLineSegment(sketch, "E0.0.454", {"start": v(-235.77, -67.02) * mm, "end": v(-237.33, -67.87) * mm});
            skLineSegment(sketch, "E0.0.455", {"start": v(-237.33, -67.87) * mm, "end": v(-240.7, -65.04) * mm});
            skLineSegment(sketch, "E0.0.456", {"start": v(-240.7, -65.04) * mm, "end": v(-240.12, -63.35) * mm});
            skLineSegment(sketch, "E0.0.457", {"start": v(-240.12, -63.35) * mm, "end": v(-239.51, -61.7) * mm});
            skLineSegment(sketch, "E0.0.458", {"start": v(-239.51, -61.7) * mm, "end": v(-238.86, -60.08) * mm});
            skLineSegment(sketch, "E0.0.459", {"start": v(-238.86, -60.08) * mm, "end": v(-238.52, -59.28) * mm});
            skLineSegment(sketch, "E0.0.460", {"start": v(-238.52, -59.28) * mm, "end": v(-238.35, -58.88) * mm});
            skLineSegment(sketch, "E0.0.461", {"start": v(-238.35, -58.88) * mm, "end": v(-238.17, -58.49) * mm});
            skLineSegment(sketch, "E0.0.462", {"start": v(-238.17, -58.49) * mm, "end": v(-241.55, -55.43) * mm});
            skLineSegment(sketch, "E0.0.463", {"start": v(-241.55, -55.43) * mm, "end": v(-241.93, -55.65) * mm});
            skLineSegment(sketch, "E0.0.464", {"start": v(-241.93, -55.65) * mm, "end": v(-242.3, -55.86) * mm});
            skLineSegment(sketch, "E0.0.465", {"start": v(-242.3, -55.86) * mm, "end": v(-243.07, -56.28) * mm});
            skLineSegment(sketch, "E0.0.466", {"start": v(-243.07, -56.28) * mm, "end": v(-244.61, -57.1) * mm});
            skLineSegment(sketch, "E0.0.467", {"start": v(-244.61, -57.1) * mm, "end": v(-246.2, -57.87) * mm});
            skLineSegment(sketch, "E0.0.468", {"start": v(-246.2, -57.87) * mm, "end": v(-247.81, -58.62) * mm});
            skLineSegment(sketch, "E0.0.469", {"start": v(-247.81, -58.62) * mm, "end": v(-250.97, -55.55) * mm});
            skLineSegment(sketch, "E0.0.470", {"start": v(-250.97, -55.55) * mm, "end": v(-250.28, -53.92) * mm});
            skLineSegment(sketch, "E0.0.471", {"start": v(-250.28, -53.92) * mm, "end": v(-249.55, -52.3) * mm});
            skLineSegment(sketch, "E0.0.472", {"start": v(-249.55, -52.3) * mm, "end": v(-248.8, -50.74) * mm});
            skLineSegment(sketch, "E0.0.473", {"start": v(-248.8, -50.74) * mm, "end": v(-248.4, -49.96) * mm});
            skLineSegment(sketch, "E0.0.474", {"start": v(-248.4, -49.96) * mm, "end": v(-248.2, -49.58) * mm});
            skLineSegment(sketch, "E0.0.475", {"start": v(-248.2, -49.58) * mm, "end": v(-248, -49.2) * mm});
            skLineSegment(sketch, "E0.0.476", {"start": v(-248, -49.2) * mm, "end": v(-251.16, -45.91) * mm});
            skLineSegment(sketch, "E0.0.477", {"start": v(-251.16, -45.91) * mm, "end": v(-251.54, -46.1) * mm});
            skLineSegment(sketch, "E0.0.478", {"start": v(-251.54, -46.1) * mm, "end": v(-251.94, -46.29) * mm});
            skLineSegment(sketch, "E0.0.479", {"start": v(-251.94, -46.29) * mm, "end": v(-252.72, -46.65) * mm});
            skLineSegment(sketch, "E0.0.480", {"start": v(-252.72, -46.65) * mm, "end": v(-254.32, -47.36) * mm});
            skLineSegment(sketch, "E0.0.481", {"start": v(-254.32, -47.36) * mm, "end": v(-255.96, -48.02) * mm});
            skLineSegment(sketch, "E0.0.482", {"start": v(-255.96, -48.02) * mm, "end": v(-257.62, -48.65) * mm});
            skLineSegment(sketch, "E0.0.483", {"start": v(-257.62, -48.65) * mm, "end": v(-260.56, -45.38) * mm});
            skLineSegment(sketch, "E0.0.484", {"start": v(-260.56, -45.38) * mm, "end": v(-259.76, -43.8) * mm});
            skLineSegment(sketch, "E0.0.485", {"start": v(-259.76, -43.8) * mm, "end": v(-258.92, -42.24) * mm});
            skLineSegment(sketch, "E0.0.486", {"start": v(-258.92, -42.24) * mm, "end": v(-258.05, -40.72) * mm});
            skLineSegment(sketch, "E0.0.487", {"start": v(-258.05, -40.72) * mm, "end": v(-257.6, -39.98) * mm});
            skLineSegment(sketch, "E0.0.488", {"start": v(-257.6, -39.98) * mm, "end": v(-257.37, -39.61) * mm});
            skLineSegment(sketch, "E0.0.489", {"start": v(-257.37, -39.61) * mm, "end": v(-257.14, -39.25) * mm});
            skLineSegment(sketch, "E0.0.490", {"start": v(-257.14, -39.25) * mm, "end": v(-260.07, -35.75) * mm});
            skLineSegment(sketch, "E0.0.491", {"start": v(-260.07, -35.75) * mm, "end": v(-260.47, -35.9) * mm});
            skLineSegment(sketch, "E0.0.492", {"start": v(-260.47, -35.9) * mm, "end": v(-260.87, -36.07) * mm});
            skLineSegment(sketch, "E0.0.493", {"start": v(-260.87, -36.07) * mm, "end": v(-261.68, -36.38) * mm});
            skLineSegment(sketch, "E0.0.494", {"start": v(-261.68, -36.38) * mm, "end": v(-263.33, -36.97) * mm});
            skLineSegment(sketch, "E0.0.495", {"start": v(-263.33, -36.97) * mm, "end": v(-265, -37.52) * mm});
            skLineSegment(sketch, "E0.0.496", {"start": v(-265, -37.52) * mm, "end": v(-266.7, -38.03) * mm});
            skLineSegment(sketch, "E0.0.497", {"start": v(-266.7, -38.03) * mm, "end": v(-269.41, -34.56) * mm});
            skLineSegment(sketch, "E0.0.498", {"start": v(-269.41, -34.56) * mm, "end": v(-268.5, -33.03) * mm});
            skLineSegment(sketch, "E0.0.499", {"start": v(-268.5, -33.03) * mm, "end": v(-267.56, -31.54) * mm});
            skLineSegment(sketch, "E0.0.500", {"start": v(-267.56, -31.54) * mm, "end": v(-266.58, -30.1) * mm});
            skLineSegment(sketch, "E0.0.501", {"start": v(-266.58, -30.1) * mm, "end": v(-266.08, -29.38) * mm});
            skLineSegment(sketch, "E0.0.502", {"start": v(-266.08, -29.38) * mm, "end": v(-265.83, -29.03) * mm});
            skLineSegment(sketch, "E0.0.503", {"start": v(-265.83, -29.03) * mm, "end": v(-265.58, -28.68) * mm});
            skLineSegment(sketch, "E0.0.504", {"start": v(-265.58, -28.68) * mm, "end": v(-268.25, -24.99) * mm});
            skLineSegment(sketch, "E0.0.505", {"start": v(-268.25, -24.99) * mm, "end": v(-268.66, -25.12) * mm});
            skLineSegment(sketch, "E0.0.506", {"start": v(-268.66, -25.12) * mm, "end": v(-269.08, -25.25) * mm});
            skLineSegment(sketch, "E0.0.507", {"start": v(-269.08, -25.25) * mm, "end": v(-269.9, -25.5) * mm});
            skLineSegment(sketch, "E0.0.508", {"start": v(-269.9, -25.5) * mm, "end": v(-271.6, -25.97) * mm});
            skLineSegment(sketch, "E0.0.509", {"start": v(-271.6, -25.97) * mm, "end": v(-273.3, -26.4) * mm});
            skLineSegment(sketch, "E0.0.510", {"start": v(-273.3, -26.4) * mm, "end": v(-275.03, -26.8) * mm});
            skLineSegment(sketch, "E0.0.511", {"start": v(-275.03, -26.8) * mm, "end": v(-277.5, -23.14) * mm});
            skLineSegment(sketch, "E0.0.512", {"start": v(-277.5, -23.14) * mm, "end": v(-276.47, -21.69) * mm});
            skLineSegment(sketch, "E0.0.513", {"start": v(-276.47, -21.69) * mm, "end": v(-275.43, -20.27) * mm});
            skLineSegment(sketch, "E0.0.514", {"start": v(-275.43, -20.27) * mm, "end": v(-274.36, -18.89) * mm});
            skLineSegment(sketch, "E0.0.515", {"start": v(-274.36, -18.89) * mm, "end": v(-273.8, -18.21) * mm});
            skLineSegment(sketch, "E0.0.516", {"start": v(-273.8, -18.21) * mm, "end": v(-273.53, -17.88) * mm});
            skLineSegment(sketch, "E0.0.517", {"start": v(-273.53, -17.88) * mm, "end": v(-273.25, -17.55) * mm});
            skLineSegment(sketch, "E0.0.518", {"start": v(-273.25, -17.55) * mm, "end": v(-275.66, -13.68) * mm});
            skLineSegment(sketch, "E0.0.519", {"start": v(-275.66, -13.68) * mm, "end": v(-276.08, -13.78) * mm});
            skLineSegment(sketch, "E0.0.520", {"start": v(-276.08, -13.78) * mm, "end": v(-276.5, -13.88) * mm});
            skLineSegment(sketch, "E0.0.521", {"start": v(-276.5, -13.88) * mm, "end": v(-277.35, -14.08) * mm});
            skLineSegment(sketch, "E0.0.522", {"start": v(-277.35, -14.08) * mm, "end": v(-279.06, -14.43) * mm});
            skLineSegment(sketch, "E0.0.523", {"start": v(-279.06, -14.43) * mm, "end": v(-280.8, -14.74) * mm});
            skLineSegment(sketch, "E0.0.524", {"start": v(-280.8, -14.74) * mm, "end": v(-282.56, -15.01) * mm});
            skLineSegment(sketch, "E0.0.525", {"start": v(-282.56, -15.01) * mm, "end": v(-284.75, -11.2) * mm});
            skLineSegment(sketch, "E0.0.526", {"start": v(-284.75, -11.2) * mm, "end": v(-283.63, -9.81) * mm});
            skLineSegment(sketch, "E0.0.527", {"start": v(-283.63, -9.81) * mm, "end": v(-282.5, -8.47) * mm});
            skLineSegment(sketch, "E0.0.528", {"start": v(-282.5, -8.47) * mm, "end": v(-281.33, -7.17) * mm});
            skLineSegment(sketch, "E0.0.529", {"start": v(-281.33, -7.17) * mm, "end": v(-280.73, -6.53) * mm});
            skLineSegment(sketch, "E0.0.530", {"start": v(-280.73, -6.53) * mm, "end": v(-280.44, -6.22) * mm});
            skLineSegment(sketch, "E0.0.531", {"start": v(-280.44, -6.22) * mm, "end": v(-280.14, -5.91) * mm});
            skLineSegment(sketch, "E0.0.532", {"start": v(-280.14, -5.91) * mm, "end": v(-282.27, -1.88) * mm});
            skLineSegment(sketch, "E0.0.533", {"start": v(-282.27, -1.88) * mm, "end": v(-282.7, -1.96) * mm});
            skLineSegment(sketch, "E0.0.534", {"start": v(-282.7, -1.96) * mm, "end": v(-283.12, -2.03) * mm});
            skLineSegment(sketch, "E0.0.535", {"start": v(-283.12, -2.03) * mm, "end": v(-283.98, -2.16) * mm});
            skLineSegment(sketch, "E0.0.536", {"start": v(-283.98, -2.16) * mm, "end": v(-285.71, -2.4) * mm});
            skLineSegment(sketch, "E0.0.537", {"start": v(-285.71, -2.4) * mm, "end": v(-287.47, -2.59) * mm});
            skLineSegment(sketch, "E0.0.538", {"start": v(-287.47, -2.59) * mm, "end": v(-289.24, -2.73) * mm});
            skLineSegment(sketch, "E0.0.539", {"start": v(-289.24, -2.73) * mm, "end": v(-291.16, 1.23) * mm});
            skLineSegment(sketch, "E0.0.540", {"start": v(-291.16, 1.23) * mm, "end": v(-289.95, 2.53) * mm});
            skLineSegment(sketch, "E0.0.541", {"start": v(-289.95, 2.53) * mm, "end": v(-288.72, 3.79) * mm});
            skLineSegment(sketch, "E0.0.542", {"start": v(-288.72, 3.79) * mm, "end": v(-287.46, 5) * mm});
            skLineSegment(sketch, "E0.0.543", {"start": v(-287.46, 5) * mm, "end": v(-286.83, 5.6) * mm});
            skLineSegment(sketch, "E0.0.544", {"start": v(-286.83, 5.6) * mm, "end": v(-286.5, 5.9) * mm});
            skLineSegment(sketch, "E0.0.545", {"start": v(-286.5, 5.9) * mm, "end": v(-286.19, 6.18) * mm});
            skLineSegment(sketch, "E0.0.546", {"start": v(-286.19, 6.18) * mm, "end": v(-288.04, 10.35) * mm});
            skLineSegment(sketch, "E0.0.547", {"start": v(-288.04, 10.35) * mm, "end": v(-288.47, 10.3) * mm});
            skLineSegment(sketch, "E0.0.548", {"start": v(-288.47, 10.3) * mm, "end": v(-288.9, 10.26) * mm});
            skLineSegment(sketch, "E0.0.549", {"start": v(-288.9, 10.26) * mm, "end": v(-289.76, 10.19) * mm});
            skLineSegment(sketch, "E0.0.550", {"start": v(-289.76, 10.19) * mm, "end": v(-291.5, 10.07) * mm});
            skLineSegment(sketch, "E0.0.551", {"start": v(-291.5, 10.07) * mm, "end": v(-293.27, 10) * mm});
            skLineSegment(sketch, "E0.0.552", {"start": v(-293.27, 10) * mm, "end": v(-295.05, 9.98) * mm});
            skLineSegment(sketch, "E0.0.553", {"start": v(-295.05, 9.98) * mm, "end": v(-296.69, 14.07) * mm});
            skLineSegment(sketch, "E0.0.554", {"start": v(-296.69, 14.07) * mm, "end": v(-295.4, 15.28) * mm});
            skLineSegment(sketch, "E0.0.555", {"start": v(-295.4, 15.28) * mm, "end": v(-294.07, 16.45) * mm});
            skLineSegment(sketch, "E0.0.556", {"start": v(-294.07, 16.45) * mm, "end": v(-292.74, 17.58) * mm});
            skLineSegment(sketch, "E0.0.557", {"start": v(-292.74, 17.58) * mm, "end": v(-292.06, 18.13) * mm});
            skLineSegment(sketch, "E0.0.558", {"start": v(-292.06, 18.13) * mm, "end": v(-291.72, 18.4) * mm});
            skLineSegment(sketch, "E0.0.559", {"start": v(-291.72, 18.4) * mm, "end": v(-291.38, 18.66) * mm});
            skLineSegment(sketch, "E0.0.560", {"start": v(-291.38, 18.66) * mm, "end": v(-292.94, 22.95) * mm});
            skLineSegment(sketch, "E0.0.561", {"start": v(-292.94, 22.95) * mm, "end": v(-293.37, 22.93) * mm});
            skLineSegment(sketch, "E0.0.562", {"start": v(-293.37, 22.93) * mm, "end": v(-293.8, 22.92) * mm});
            skLineSegment(sketch, "E0.0.563", {"start": v(-293.8, 22.92) * mm, "end": v(-294.67, 22.9) * mm});
            skLineSegment(sketch, "E0.0.564", {"start": v(-294.67, 22.9) * mm, "end": v(-296.42, 22.92) * mm});
            skLineSegment(sketch, "E0.0.565", {"start": v(-296.42, 22.92) * mm, "end": v(-298.18, 22.97) * mm});
            skLineSegment(sketch, "E0.0.566", {"start": v(-298.18, 22.97) * mm, "end": v(-299.95, 23.07) * mm});
            skLineSegment(sketch, "E0.0.567", {"start": v(-299.95, 23.07) * mm, "end": v(-301.3, 27.26) * mm});
            skLineSegment(sketch, "E0.0.568", {"start": v(-301.3, 27.26) * mm, "end": v(-299.93, 28.38) * mm});
            skLineSegment(sketch, "E0.0.569", {"start": v(-299.93, 28.38) * mm, "end": v(-298.53, 29.46) * mm});
            skLineSegment(sketch, "E0.0.570", {"start": v(-298.53, 29.46) * mm, "end": v(-297.12, 30.5) * mm});
            skLineSegment(sketch, "E0.0.571", {"start": v(-297.12, 30.5) * mm, "end": v(-296.4, 31) * mm});
            skLineSegment(sketch, "E0.0.572", {"start": v(-296.4, 31) * mm, "end": v(-296.05, 31.24) * mm});
            skLineSegment(sketch, "E0.0.573", {"start": v(-296.05, 31.24) * mm, "end": v(-295.7, 31.48) * mm});
            skLineSegment(sketch, "E0.0.574", {"start": v(-295.7, 31.48) * mm, "end": v(-296.94, 35.86) * mm});
            skLineSegment(sketch, "E0.0.575", {"start": v(-296.94, 35.86) * mm, "end": v(-297.38, 35.88) * mm});
            skLineSegment(sketch, "E0.0.576", {"start": v(-297.38, 35.88) * mm, "end": v(-297.8, 35.9) * mm});
            skLineSegment(sketch, "E0.0.577", {"start": v(-297.8, 35.9) * mm, "end": v(-298.68, 35.94) * mm});
            skLineSegment(sketch, "E0.0.578", {"start": v(-298.68, 35.94) * mm, "end": v(-300.42, 36.07) * mm});
            skLineSegment(sketch, "E0.0.579", {"start": v(-300.42, 36.07) * mm, "end": v(-302.17, 36.25) * mm});
            skLineSegment(sketch, "E0.0.580", {"start": v(-302.17, 36.25) * mm, "end": v(-303.94, 36.48) * mm});
            skLineSegment(sketch, "E0.0.581", {"start": v(-303.94, 36.48) * mm, "end": v(-305, 40.75) * mm});
            skLineSegment(sketch, "E0.0.582", {"start": v(-305, 40.75) * mm, "end": v(-303.54, 41.77) * mm});
            skLineSegment(sketch, "E0.0.583", {"start": v(-303.54, 41.77) * mm, "end": v(-302.07, 42.75) * mm});
            skLineSegment(sketch, "E0.0.584", {"start": v(-302.07, 42.75) * mm, "end": v(-300.6, 43.68) * mm});
            skLineSegment(sketch, "E0.0.585", {"start": v(-300.6, 43.68) * mm, "end": v(-299.85, 44.13) * mm});
            skLineSegment(sketch, "E0.0.586", {"start": v(-299.85, 44.13) * mm, "end": v(-299.47, 44.34) * mm});
            skLineSegment(sketch, "E0.0.587", {"start": v(-299.47, 44.34) * mm, "end": v(-299.1, 44.56) * mm});
            skLineSegment(sketch, "E0.0.588", {"start": v(-299.1, 44.56) * mm, "end": v(-300.04, 49.02) * mm});
            skLineSegment(sketch, "E0.0.589", {"start": v(-300.04, 49.02) * mm, "end": v(-300.47, 49.07) * mm});
            skLineSegment(sketch, "E0.0.590", {"start": v(-300.47, 49.07) * mm, "end": v(-300.9, 49.12) * mm});
            skLineSegment(sketch, "E0.0.591", {"start": v(-300.9, 49.12) * mm, "end": v(-301.76, 49.22) * mm});
            skLineSegment(sketch, "E0.0.592", {"start": v(-301.76, 49.22) * mm, "end": v(-303.5, 49.48) * mm});
            skLineSegment(sketch, "E0.0.593", {"start": v(-303.5, 49.48) * mm, "end": v(-305.23, 49.78) * mm});
            skLineSegment(sketch, "E0.0.594", {"start": v(-305.23, 49.78) * mm, "end": v(-306.97, 50.12) * mm});
            skLineSegment(sketch, "E0.0.595", {"start": v(-306.97, 50.12) * mm, "end": v(-307.73, 54.46) * mm});
            skLineSegment(sketch, "E0.0.596", {"start": v(-307.73, 54.46) * mm, "end": v(-306.2, 55.38) * mm});
            skLineSegment(sketch, "E0.0.597", {"start": v(-306.2, 55.38) * mm, "end": v(-304.68, 56.25) * mm});
            skLineSegment(sketch, "E0.0.598", {"start": v(-304.68, 56.25) * mm, "end": v(-303.14, 57.07) * mm});
            skLineSegment(sketch, "E0.0.599", {"start": v(-303.14, 57.07) * mm, "end": v(-302.36, 57.47) * mm});
            skLineSegment(sketch, "E0.0.600", {"start": v(-302.36, 57.47) * mm, "end": v(-301.97, 57.66) * mm});
            skLineSegment(sketch, "E0.0.601", {"start": v(-301.97, 57.66) * mm, "end": v(-301.59, 57.85) * mm});
            skLineSegment(sketch, "E0.0.602", {"start": v(-301.59, 57.85) * mm, "end": v(-302.21, 62.37) * mm});
            skLineSegment(sketch, "E0.0.603", {"start": v(-302.21, 62.37) * mm, "end": v(-302.64, 62.44) * mm});
            skLineSegment(sketch, "E0.0.604", {"start": v(-302.64, 62.44) * mm, "end": v(-303.06, 62.52) * mm});
            skLineSegment(sketch, "E0.0.605", {"start": v(-303.06, 62.52) * mm, "end": v(-303.92, 62.69) * mm});
            skLineSegment(sketch, "E0.0.606", {"start": v(-303.92, 62.69) * mm, "end": v(-305.62, 63.06) * mm});
            skLineSegment(sketch, "E0.0.607", {"start": v(-305.62, 63.06) * mm, "end": v(-307.34, 63.48) * mm});
            skLineSegment(sketch, "E0.0.608", {"start": v(-307.34, 63.48) * mm, "end": v(-309.05, 63.95) * mm});
            skLineSegment(sketch, "E0.0.609", {"start": v(-309.05, 63.95) * mm, "end": v(-309.5, 68.33) * mm});
            skLineSegment(sketch, "E0.0.610", {"start": v(-309.5, 68.33) * mm, "end": v(-307.92, 69.14) * mm});
            skLineSegment(sketch, "E0.0.611", {"start": v(-307.92, 69.14) * mm, "end": v(-306.33, 69.9) * mm});
            skLineSegment(sketch, "E0.0.612", {"start": v(-306.33, 69.9) * mm, "end": v(-304.74, 70.62) * mm});
            skLineSegment(sketch, "E0.0.613", {"start": v(-304.74, 70.62) * mm, "end": v(-303.94, 70.95) * mm});
            skLineSegment(sketch, "E0.0.614", {"start": v(-303.94, 70.95) * mm, "end": v(-303.54, 71.12) * mm});
            skLineSegment(sketch, "E0.0.615", {"start": v(-303.54, 71.12) * mm, "end": v(-303.14, 71.28) * mm});
            skLineSegment(sketch, "E0.0.616", {"start": v(-303.14, 71.28) * mm, "end": v(-303.45, 75.83) * mm});
            skLineSegment(sketch, "E0.0.617", {"start": v(-303.45, 75.83) * mm, "end": v(-303.87, 75.93) * mm});
            skLineSegment(sketch, "E0.0.618", {"start": v(-303.87, 75.93) * mm, "end": v(-304.29, 76.04) * mm});
            skLineSegment(sketch, "E0.0.619", {"start": v(-304.29, 76.04) * mm, "end": v(-305.13, 76.27) * mm});
            skLineSegment(sketch, "E0.0.620", {"start": v(-305.13, 76.27) * mm, "end": v(-306.8, 76.76) * mm});
            skLineSegment(sketch, "E0.0.621", {"start": v(-306.8, 76.76) * mm, "end": v(-308.48, 77.3) * mm});
            skLineSegment(sketch, "E0.0.622", {"start": v(-308.48, 77.3) * mm, "end": v(-310.16, 77.88) * mm});
            skLineSegment(sketch, "E0.0.623", {"start": v(-310.16, 77.88) * mm, "end": v(-310.3, 82.29) * mm});
            skLineSegment(sketch, "E0.0.624", {"start": v(-310.3, 82.29) * mm, "end": v(-308.67, 82.98) * mm});
            skLineSegment(sketch, "E0.0.625", {"start": v(-308.67, 82.98) * mm, "end": v(-307.03, 83.63) * mm});
            skLineSegment(sketch, "E0.0.626", {"start": v(-307.03, 83.63) * mm, "end": v(-305.4, 84.23) * mm});
            skLineSegment(sketch, "E0.0.627", {"start": v(-305.4, 84.23) * mm, "end": v(-304.57, 84.52) * mm});
            skLineSegment(sketch, "E0.0.628", {"start": v(-304.57, 84.52) * mm, "end": v(-304.16, 84.65) * mm});
            skLineSegment(sketch, "E0.0.629", {"start": v(-304.16, 84.65) * mm, "end": v(-303.75, 84.79) * mm});
            skLineSegment(sketch, "E0.0.630", {"start": v(-303.75, 84.79) * mm, "end": v(-303.74, 89.35) * mm});
            skLineSegment(sketch, "E0.0.631", {"start": v(-303.74, 89.35) * mm, "end": v(-304.15, 89.48) * mm});
            skLineSegment(sketch, "E0.0.632", {"start": v(-304.15, 89.48) * mm, "end": v(-304.57, 89.62) * mm});
            skLineSegment(sketch, "E0.0.633", {"start": v(-304.57, 89.62) * mm, "end": v(-305.39, 89.9) * mm});
            skLineSegment(sketch, "E0.0.634", {"start": v(-305.39, 89.9) * mm, "end": v(-307.03, 90.5) * mm});
            skLineSegment(sketch, "E0.0.635", {"start": v(-307.03, 90.5) * mm, "end": v(-308.66, 91.16) * mm});
            skLineSegment(sketch, "E0.0.636", {"start": v(-308.66, 91.16) * mm, "end": v(-310.3, 91.86) * mm});
            skLineSegment(sketch, "E0.0.637", {"start": v(-310.3, 91.86) * mm, "end": v(-310.14, 96.27) * mm});
            skLineSegment(sketch, "E0.0.638", {"start": v(-310.14, 96.27) * mm, "end": v(-308.46, 96.85) * mm});
            skLineSegment(sketch, "E0.0.639", {"start": v(-308.46, 96.85) * mm, "end": v(-306.78, 97.38) * mm});
            skLineSegment(sketch, "E0.0.640", {"start": v(-306.78, 97.38) * mm, "end": v(-305.1, 97.87) * mm});
            skLineSegment(sketch, "E0.0.641", {"start": v(-305.1, 97.87) * mm, "end": v(-304.26, 98.1) * mm});
            skLineSegment(sketch, "E0.0.642", {"start": v(-304.26, 98.1) * mm, "end": v(-303.84, 98.2) * mm});
            skLineSegment(sketch, "E0.0.643", {"start": v(-303.84, 98.2) * mm, "end": v(-303.42, 98.3) * mm});
            skLineSegment(sketch, "E0.0.644", {"start": v(-303.42, 98.3) * mm, "end": v(-303.1, 102.85) * mm});
            skLineSegment(sketch, "E0.0.645", {"start": v(-303.1, 102.85) * mm, "end": v(-303.5, 103.01) * mm});
            skLineSegment(sketch, "E0.0.646", {"start": v(-303.5, 103.01) * mm, "end": v(-303.9, 103.18) * mm});
            skLineSegment(sketch, "E0.0.647", {"start": v(-303.9, 103.18) * mm, "end": v(-304.7, 103.52) * mm});
            skLineSegment(sketch, "E0.0.648", {"start": v(-304.7, 103.52) * mm, "end": v(-306.29, 104.24) * mm});
            skLineSegment(sketch, "E0.0.649", {"start": v(-306.29, 104.24) * mm, "end": v(-307.87, 105) * mm});
            skLineSegment(sketch, "E0.0.650", {"start": v(-307.87, 105) * mm, "end": v(-309.45, 105.82) * mm});
            skLineSegment(sketch, "E0.0.651", {"start": v(-309.45, 105.82) * mm, "end": v(-308.99, 110.2) * mm});
            skLineSegment(sketch, "E0.0.652", {"start": v(-308.99, 110.2) * mm, "end": v(-307.27, 110.66) * mm});
            skLineSegment(sketch, "E0.0.653", {"start": v(-307.27, 110.66) * mm, "end": v(-305.56, 111.08) * mm});
            skLineSegment(sketch, "E0.0.654", {"start": v(-305.56, 111.08) * mm, "end": v(-303.85, 111.44) * mm});
            skLineSegment(sketch, "E0.0.655", {"start": v(-303.85, 111.44) * mm, "end": v(-303, 111.61) * mm});
            skLineSegment(sketch, "E0.0.656", {"start": v(-303, 111.61) * mm, "end": v(-302.57, 111.69) * mm});
            skLineSegment(sketch, "E0.0.657", {"start": v(-302.57, 111.69) * mm, "end": v(-302.14, 111.76) * mm});
            skLineSegment(sketch, "E0.0.658", {"start": v(-302.14, 111.76) * mm, "end": v(-301.5, 116.28) * mm});
            skLineSegment(sketch, "E0.0.659", {"start": v(-301.5, 116.28) * mm, "end": v(-301.9, 116.47) * mm});
            skLineSegment(sketch, "E0.0.660", {"start": v(-301.9, 116.47) * mm, "end": v(-302.28, 116.66) * mm});
            skLineSegment(sketch, "E0.0.661", {"start": v(-302.28, 116.66) * mm, "end": v(-303.05, 117.06) * mm});
            skLineSegment(sketch, "E0.0.662", {"start": v(-303.05, 117.06) * mm, "end": v(-304.6, 117.88) * mm});
            skLineSegment(sketch, "E0.0.663", {"start": v(-304.6, 117.88) * mm, "end": v(-306.12, 118.76) * mm});
            skLineSegment(sketch, "E0.0.664", {"start": v(-306.12, 118.76) * mm, "end": v(-307.64, 119.68) * mm});
            skLineSegment(sketch, "E0.0.665", {"start": v(-307.64, 119.68) * mm, "end": v(-306.87, 124.02) * mm});
            skLineSegment(sketch, "E0.0.666", {"start": v(-306.87, 124.02) * mm, "end": v(-305.13, 124.36) * mm});
            skLineSegment(sketch, "E0.0.667", {"start": v(-305.13, 124.36) * mm, "end": v(-303.39, 124.65) * mm});
            skLineSegment(sketch, "E0.0.668", {"start": v(-303.39, 124.65) * mm, "end": v(-301.66, 124.9) * mm});
            skLineSegment(sketch, "E0.0.669", {"start": v(-301.66, 124.9) * mm, "end": v(-300.8, 125) * mm});
            skLineSegment(sketch, "E0.0.670", {"start": v(-300.8, 125) * mm, "end": v(-300.37, 125.06) * mm});
            skLineSegment(sketch, "E0.0.671", {"start": v(-300.37, 125.06) * mm, "end": v(-299.94, 125.1) * mm});
            skLineSegment(sketch, "E0.0.672", {"start": v(-299.94, 125.1) * mm, "end": v(-298.98, 129.56) * mm});
            skLineSegment(sketch, "E0.0.673", {"start": v(-298.98, 129.56) * mm, "end": v(-299.36, 129.78) * mm});
            skLineSegment(sketch, "E0.0.674", {"start": v(-299.36, 129.78) * mm, "end": v(-299.73, 130) * mm});
            skLineSegment(sketch, "E0.0.675", {"start": v(-299.73, 130) * mm, "end": v(-300.47, 130.44) * mm});
            skLineSegment(sketch, "E0.0.676", {"start": v(-300.47, 130.44) * mm, "end": v(-301.95, 131.38) * mm});
            skLineSegment(sketch, "E0.0.677", {"start": v(-301.95, 131.38) * mm, "end": v(-303.41, 132.36) * mm});
            skLineSegment(sketch, "E0.0.678", {"start": v(-303.41, 132.36) * mm, "end": v(-304.87, 133.39) * mm});
            skLineSegment(sketch, "E0.0.679", {"start": v(-304.87, 133.39) * mm, "end": v(-303.8, 137.66) * mm});
            skLineSegment(sketch, "E0.0.680", {"start": v(-303.8, 137.66) * mm, "end": v(-302.03, 137.87) * mm});
            skLineSegment(sketch, "E0.0.681", {"start": v(-302.03, 137.87) * mm, "end": v(-300.28, 138.05) * mm});
            skLineSegment(sketch, "E0.0.682", {"start": v(-300.28, 138.05) * mm, "end": v(-298.53, 138.18) * mm});
            skLineSegment(sketch, "E0.0.683", {"start": v(-298.53, 138.18) * mm, "end": v(-297.67, 138.22) * mm});
            skLineSegment(sketch, "E0.0.684", {"start": v(-297.67, 138.22) * mm, "end": v(-297.23, 138.24) * mm});
            skLineSegment(sketch, "E0.0.685", {"start": v(-297.23, 138.24) * mm, "end": v(-296.8, 138.25) * mm});
            skLineSegment(sketch, "E0.0.686", {"start": v(-296.8, 138.25) * mm, "end": v(-295.54, 142.63) * mm});
            skLineSegment(sketch, "E0.0.687", {"start": v(-295.54, 142.63) * mm, "end": v(-295.9, 142.88) * mm});
            skLineSegment(sketch, "E0.0.688", {"start": v(-295.9, 142.88) * mm, "end": v(-296.25, 143.12) * mm});
            skLineSegment(sketch, "E0.0.689", {"start": v(-296.25, 143.12) * mm, "end": v(-296.96, 143.62) * mm});
            skLineSegment(sketch, "E0.0.690", {"start": v(-296.96, 143.62) * mm, "end": v(-298.37, 144.66) * mm});
            skLineSegment(sketch, "E0.0.691", {"start": v(-298.37, 144.66) * mm, "end": v(-299.76, 145.74) * mm});
            skLineSegment(sketch, "E0.0.692", {"start": v(-299.76, 145.74) * mm, "end": v(-301.14, 146.86) * mm});
            skLineSegment(sketch, "E0.0.693", {"start": v(-301.14, 146.86) * mm, "end": v(-299.77, 151.05) * mm});
            skLineSegment(sketch, "E0.0.694", {"start": v(-299.77, 151.05) * mm, "end": v(-298, 151.14) * mm});
            skLineSegment(sketch, "E0.0.695", {"start": v(-298, 151.14) * mm, "end": v(-296.24, 151.2) * mm});
            skLineSegment(sketch, "E0.0.696", {"start": v(-296.24, 151.2) * mm, "end": v(-294.49, 151.2) * mm});
            skLineSegment(sketch, "E0.0.697", {"start": v(-294.49, 151.2) * mm, "end": v(-293.62, 151.18) * mm});
            skLineSegment(sketch, "E0.0.698", {"start": v(-293.62, 151.18) * mm, "end": v(-293.19, 151.17) * mm});
            skLineSegment(sketch, "E0.0.699", {"start": v(-293.19, 151.17) * mm, "end": v(-292.76, 151.15) * mm});
            skLineSegment(sketch, "E0.0.700", {"start": v(-292.76, 151.15) * mm, "end": v(-291.2, 155.44) * mm});
            skLineSegment(sketch, "E0.0.701", {"start": v(-291.2, 155.44) * mm, "end": v(-291.53, 155.7) * mm});
            skLineSegment(sketch, "E0.0.702", {"start": v(-291.53, 155.7) * mm, "end": v(-291.87, 155.97) * mm});
            skLineSegment(sketch, "E0.0.703", {"start": v(-291.87, 155.97) * mm, "end": v(-292.54, 156.52) * mm});
            skLineSegment(sketch, "E0.0.704", {"start": v(-292.54, 156.52) * mm, "end": v(-293.88, 157.65) * mm});
            skLineSegment(sketch, "E0.0.705", {"start": v(-293.88, 157.65) * mm, "end": v(-295.2, 158.83) * mm});
            skLineSegment(sketch, "E0.0.706", {"start": v(-295.2, 158.83) * mm, "end": v(-296.49, 160.04) * mm});
            skLineSegment(sketch, "E0.0.707", {"start": v(-296.49, 160.04) * mm, "end": v(-294.83, 164.12) * mm});
            skLineSegment(sketch, "E0.0.708", {"start": v(-294.83, 164.12) * mm, "end": v(-293.05, 164.1) * mm});
            skLineSegment(sketch, "E0.0.709", {"start": v(-293.05, 164.1) * mm, "end": v(-291.3, 164.02) * mm});
            skLineSegment(sketch, "E0.0.710", {"start": v(-291.3, 164.02) * mm, "end": v(-289.55, 163.9) * mm});
            skLineSegment(sketch, "E0.0.711", {"start": v(-289.55, 163.9) * mm, "end": v(-288.68, 163.83) * mm});
            skLineSegment(sketch, "E0.0.712", {"start": v(-288.68, 163.83) * mm, "end": v(-288.25, 163.79) * mm});
            skLineSegment(sketch, "E0.0.713", {"start": v(-288.25, 163.79) * mm, "end": v(-287.82, 163.74) * mm});
            skLineSegment(sketch, "E0.0.714", {"start": v(-287.82, 163.74) * mm, "end": v(-285.96, 167.9) * mm});
            skLineSegment(sketch, "E0.0.715", {"start": v(-285.96, 167.9) * mm, "end": v(-286.28, 168.2) * mm});
            skLineSegment(sketch, "E0.0.716", {"start": v(-286.28, 168.2) * mm, "end": v(-286.6, 168.49) * mm});
            skLineSegment(sketch, "E0.0.717", {"start": v(-286.6, 168.49) * mm, "end": v(-287.24, 169.08) * mm});
            skLineSegment(sketch, "E0.0.718", {"start": v(-287.24, 169.08) * mm, "end": v(-288.49, 170.3) * mm});
            skLineSegment(sketch, "E0.0.719", {"start": v(-288.49, 170.3) * mm, "end": v(-289.72, 171.56) * mm});
            skLineSegment(sketch, "E0.0.720", {"start": v(-289.72, 171.56) * mm, "end": v(-290.92, 172.87) * mm});
            skLineSegment(sketch, "E0.0.721", {"start": v(-290.92, 172.87) * mm, "end": v(-288.99, 176.82) * mm});
            skLineSegment(sketch, "E0.0.722", {"start": v(-288.99, 176.82) * mm, "end": v(-287.22, 176.67) * mm});
            skLineSegment(sketch, "E0.0.723", {"start": v(-287.22, 176.67) * mm, "end": v(-285.46, 176.48) * mm});
            skLineSegment(sketch, "E0.0.724", {"start": v(-285.46, 176.48) * mm, "end": v(-283.73, 176.24) * mm});
            skLineSegment(sketch, "E0.0.725", {"start": v(-283.73, 176.24) * mm, "end": v(-282.87, 176.1) * mm});
            skLineSegment(sketch, "E0.0.726", {"start": v(-282.87, 176.1) * mm, "end": v(-282.45, 176.03) * mm});
            skLineSegment(sketch, "E0.0.727", {"start": v(-282.45, 176.03) * mm, "end": v(-282.02, 175.95) * mm});
            skLineSegment(sketch, "E0.0.728", {"start": v(-282.02, 175.95) * mm, "end": v(-279.88, 179.98) * mm});
            skLineSegment(sketch, "E0.0.729", {"start": v(-279.88, 179.98) * mm, "end": v(-280.18, 180.29) * mm});
            skLineSegment(sketch, "E0.0.730", {"start": v(-280.18, 180.29) * mm, "end": v(-280.47, 180.6) * mm});
            skLineSegment(sketch, "E0.0.731", {"start": v(-280.47, 180.6) * mm, "end": v(-281.06, 181.24) * mm});
            skLineSegment(sketch, "E0.0.732", {"start": v(-281.06, 181.24) * mm, "end": v(-282.23, 182.54) * mm});
            skLineSegment(sketch, "E0.0.733", {"start": v(-282.23, 182.54) * mm, "end": v(-283.36, 183.9) * mm});
            skLineSegment(sketch, "E0.0.734", {"start": v(-283.36, 183.9) * mm, "end": v(-284.48, 185.28) * mm});
            skLineSegment(sketch, "E0.0.735", {"start": v(-284.48, 185.28) * mm, "end": v(-282.27, 189.09) * mm});
            skLineSegment(sketch, "E0.0.736", {"start": v(-282.27, 189.09) * mm, "end": v(-280.51, 188.81) * mm});
            skLineSegment(sketch, "E0.0.737", {"start": v(-280.51, 188.81) * mm, "end": v(-278.78, 188.5) * mm});
            skLineSegment(sketch, "E0.0.738", {"start": v(-278.78, 188.5) * mm, "end": v(-277.07, 188.13) * mm});
            skLineSegment(sketch, "E0.0.739", {"start": v(-277.07, 188.13) * mm, "end": v(-276.22, 187.94) * mm});
            skLineSegment(sketch, "E0.0.740", {"start": v(-276.22, 187.94) * mm, "end": v(-275.8, 187.84) * mm});
            skLineSegment(sketch, "E0.0.741", {"start": v(-275.8, 187.84) * mm, "end": v(-275.38, 187.73) * mm});
            skLineSegment(sketch, "E0.0.742", {"start": v(-275.38, 187.73) * mm, "end": v(-272.96, 191.6) * mm});
            skLineSegment(sketch, "E0.0.743", {"start": v(-272.96, 191.6) * mm, "end": v(-273.24, 191.93) * mm});
            skLineSegment(sketch, "E0.0.744", {"start": v(-273.24, 191.93) * mm, "end": v(-273.51, 192.26) * mm});
            skLineSegment(sketch, "E0.0.745", {"start": v(-273.51, 192.26) * mm, "end": v(-274.06, 192.94) * mm});
            skLineSegment(sketch, "E0.0.746", {"start": v(-274.06, 192.94) * mm, "end": v(-275.13, 194.32) * mm});
            skLineSegment(sketch, "E0.0.747", {"start": v(-275.13, 194.32) * mm, "end": v(-276.17, 195.74) * mm});
            skLineSegment(sketch, "E0.0.748", {"start": v(-276.17, 195.74) * mm, "end": v(-277.18, 197.2) * mm});
            skLineSegment(sketch, "E0.0.749", {"start": v(-277.18, 197.2) * mm, "end": v(-274.72, 200.85) * mm});
            skLineSegment(sketch, "E0.0.750", {"start": v(-274.72, 200.85) * mm, "end": v(-272.98, 200.45) * mm});
            skLineSegment(sketch, "E0.0.751", {"start": v(-272.98, 200.45) * mm, "end": v(-271.28, 200.02) * mm});
            skLineSegment(sketch, "E0.0.752", {"start": v(-271.28, 200.02) * mm, "end": v(-269.6, 199.54) * mm});
            skLineSegment(sketch, "E0.0.753", {"start": v(-269.6, 199.54) * mm, "end": v(-268.76, 199.28) * mm});
            skLineSegment(sketch, "E0.0.754", {"start": v(-268.76, 199.28) * mm, "end": v(-268.35, 199.15) * mm});
            skLineSegment(sketch, "E0.0.755", {"start": v(-268.35, 199.15) * mm, "end": v(-267.94, 199.02) * mm});
            skLineSegment(sketch, "E0.0.756", {"start": v(-267.94, 199.02) * mm, "end": v(-265.25, 202.7) * mm});
            skLineSegment(sketch, "E0.0.757", {"start": v(-265.25, 202.7) * mm, "end": v(-265.5, 203.05) * mm});
            skLineSegment(sketch, "E0.0.758", {"start": v(-265.5, 203.05) * mm, "end": v(-265.76, 203.4) * mm});
            skLineSegment(sketch, "E0.0.759", {"start": v(-265.76, 203.4) * mm, "end": v(-266.26, 204.12) * mm});
            skLineSegment(sketch, "E0.0.760", {"start": v(-266.26, 204.12) * mm, "end": v(-267.23, 205.57) * mm});
            skLineSegment(sketch, "E0.0.761", {"start": v(-267.23, 205.57) * mm, "end": v(-268.16, 207.06) * mm});
            skLineSegment(sketch, "E0.0.762", {"start": v(-268.16, 207.06) * mm, "end": v(-269.07, 208.6) * mm});
            skLineSegment(sketch, "E0.0.763", {"start": v(-269.07, 208.6) * mm, "end": v(-266.36, 212.06) * mm});
            skLineSegment(sketch, "E0.0.764", {"start": v(-266.36, 212.06) * mm, "end": v(-264.66, 211.54) * mm});
            skLineSegment(sketch, "E0.0.765", {"start": v(-264.66, 211.54) * mm, "end": v(-262.98, 210.99) * mm});
            skLineSegment(sketch, "E0.0.766", {"start": v(-262.98, 210.99) * mm, "end": v(-261.34, 210.4) * mm});
            skLineSegment(sketch, "E0.0.767", {"start": v(-261.34, 210.4) * mm, "end": v(-260.53, 210.08) * mm});
            skLineSegment(sketch, "E0.0.768", {"start": v(-260.53, 210.08) * mm, "end": v(-260.13, 209.92) * mm});
            skLineSegment(sketch, "E0.0.769", {"start": v(-260.13, 209.92) * mm, "end": v(-259.73, 209.76) * mm});
            skLineSegment(sketch, "E0.0.770", {"start": v(-259.73, 209.76) * mm, "end": v(-256.8, 213.25) * mm});
            skLineSegment(sketch, "E0.0.771", {"start": v(-256.8, 213.25) * mm, "end": v(-257.02, 213.61) * mm});
            skLineSegment(sketch, "E0.0.772", {"start": v(-257.02, 213.61) * mm, "end": v(-257.25, 213.98) * mm});
            skLineSegment(sketch, "E0.0.773", {"start": v(-257.25, 213.98) * mm, "end": v(-257.7, 214.73) * mm});
            skLineSegment(sketch, "E0.0.774", {"start": v(-257.7, 214.73) * mm, "end": v(-258.56, 216.25) * mm});
            skLineSegment(sketch, "E0.0.775", {"start": v(-258.56, 216.25) * mm, "end": v(-259.39, 217.8) * mm});
            skLineSegment(sketch, "E0.0.776", {"start": v(-259.39, 217.8) * mm, "end": v(-260.2, 219.39) * mm});
            skLineSegment(sketch, "E0.0.777", {"start": v(-260.2, 219.39) * mm, "end": v(-257.24, 222.66) * mm});
            skLineSegment(sketch, "E0.0.778", {"start": v(-257.24, 222.66) * mm, "end": v(-255.58, 222.02) * mm});
            skLineSegment(sketch, "E0.0.779", {"start": v(-255.58, 222.02) * mm, "end": v(-253.95, 221.35) * mm});
            skLineSegment(sketch, "E0.0.780", {"start": v(-253.95, 221.35) * mm, "end": v(-252.35, 220.64) * mm});
            skLineSegment(sketch, "E0.0.781", {"start": v(-252.35, 220.64) * mm, "end": v(-251.56, 220.28) * mm});
            skLineSegment(sketch, "E0.0.782", {"start": v(-251.56, 220.28) * mm, "end": v(-251.17, 220.09) * mm});
            skLineSegment(sketch, "E0.0.783", {"start": v(-251.17, 220.09) * mm, "end": v(-250.78, 219.9) * mm});
            skLineSegment(sketch, "E0.0.784", {"start": v(-250.78, 219.9) * mm, "end": v(-247.61, 223.17) * mm});
            skLineSegment(sketch, "E0.0.785", {"start": v(-247.61, 223.17) * mm, "end": v(-247.82, 223.56) * mm});
            skLineSegment(sketch, "E0.0.786", {"start": v(-247.82, 223.56) * mm, "end": v(-248.02, 223.94) * mm});
            skLineSegment(sketch, "E0.0.787", {"start": v(-248.02, 223.94) * mm, "end": v(-248.4, 224.71) * mm});
            skLineSegment(sketch, "E0.0.788", {"start": v(-248.4, 224.71) * mm, "end": v(-249.17, 226.29) * mm});
            skLineSegment(sketch, "E0.0.789", {"start": v(-249.17, 226.29) * mm, "end": v(-249.89, 227.9) * mm});
            skLineSegment(sketch, "E0.0.790", {"start": v(-249.89, 227.9) * mm, "end": v(-250.58, 229.54) * mm});
            skLineSegment(sketch, "E0.0.791", {"start": v(-250.58, 229.54) * mm, "end": v(-247.4, 232.6) * mm});
            skLineSegment(sketch, "E0.0.792", {"start": v(-247.4, 232.6) * mm, "end": v(-245.8, 231.84) * mm});
            skLineSegment(sketch, "E0.0.793", {"start": v(-245.8, 231.84) * mm, "end": v(-244.21, 231.06) * mm});
            skLineSegment(sketch, "E0.0.794", {"start": v(-244.21, 231.06) * mm, "end": v(-242.67, 230.24) * mm});
            skLineSegment(sketch, "E0.0.795", {"start": v(-242.67, 230.24) * mm, "end": v(-241.9, 229.82) * mm});
            skLineSegment(sketch, "E0.0.796", {"start": v(-241.9, 229.82) * mm, "end": v(-241.53, 229.6) * mm});
            skLineSegment(sketch, "E0.0.797", {"start": v(-241.53, 229.6) * mm, "end": v(-241.16, 229.4) * mm});
            skLineSegment(sketch, "E0.0.798", {"start": v(-241.16, 229.4) * mm, "end": v(-237.76, 232.44) * mm});
            skLineSegment(sketch, "E0.0.799", {"start": v(-237.76, 232.44) * mm, "end": v(-237.94, 232.83) * mm});
            skLineSegment(sketch, "E0.0.800", {"start": v(-237.94, 232.83) * mm, "end": v(-238.11, 233.23) * mm});
            skLineSegment(sketch, "E0.0.801", {"start": v(-238.11, 233.23) * mm, "end": v(-238.45, 234.03) * mm});
            skLineSegment(sketch, "E0.0.802", {"start": v(-238.45, 234.03) * mm, "end": v(-239.1, 235.65) * mm});
            skLineSegment(sketch, "E0.0.803", {"start": v(-239.1, 235.65) * mm, "end": v(-239.7, 237.3) * mm});
            skLineSegment(sketch, "E0.0.804", {"start": v(-239.7, 237.3) * mm, "end": v(-240.28, 239) * mm});
            skLineSegment(sketch, "E0.0.805", {"start": v(-240.28, 239) * mm, "end": v(-236.9, 241.82) * mm});
            skLineSegment(sketch, "E0.0.806", {"start": v(-236.9, 241.82) * mm, "end": v(-235.34, 240.96) * mm});
            skLineSegment(sketch, "E0.0.807", {"start": v(-235.34, 240.96) * mm, "end": v(-233.82, 240.07) * mm});
            skLineSegment(sketch, "E0.0.808", {"start": v(-233.82, 240.07) * mm, "end": v(-232.34, 239.14) * mm});
            skLineSegment(sketch, "E0.0.809", {"start": v(-232.34, 239.14) * mm, "end": v(-231.6, 238.67) * mm});
            skLineSegment(sketch, "E0.0.810", {"start": v(-231.6, 238.67) * mm, "end": v(-231.25, 238.43) * mm});
            skLineSegment(sketch, "E0.0.811", {"start": v(-231.25, 238.43) * mm, "end": v(-230.9, 238.19) * mm});
            skLineSegment(sketch, "E0.0.812", {"start": v(-230.9, 238.19) * mm, "end": v(-227.3, 241) * mm});
            skLineSegment(sketch, "E0.0.813", {"start": v(-227.3, 241) * mm, "end": v(-227.44, 241.4) * mm});
            skLineSegment(sketch, "E0.0.814", {"start": v(-227.44, 241.4) * mm, "end": v(-227.59, 241.8) * mm});
            skLineSegment(sketch, "E0.0.815", {"start": v(-227.59, 241.8) * mm, "end": v(-227.87, 242.63) * mm});
            skLineSegment(sketch, "E0.0.816", {"start": v(-227.87, 242.63) * mm, "end": v(-228.4, 244.3) * mm});
            skLineSegment(sketch, "E0.0.817", {"start": v(-228.4, 244.3) * mm, "end": v(-228.89, 245.99) * mm});
            skLineSegment(sketch, "E0.0.818", {"start": v(-228.89, 245.99) * mm, "end": v(-229.34, 247.7) * mm});
            skLineSegment(sketch, "E0.0.819", {"start": v(-229.34, 247.7) * mm, "end": v(-225.78, 250.29) * mm});
            skLineSegment(sketch, "E0.0.820", {"start": v(-225.78, 250.29) * mm, "end": v(-224.28, 249.32) * mm});
            skLineSegment(sketch, "E0.0.821", {"start": v(-224.28, 249.32) * mm, "end": v(-222.83, 248.33) * mm});
            skLineSegment(sketch, "E0.0.822", {"start": v(-222.83, 248.33) * mm, "end": v(-221.41, 247.3) * mm});
            skLineSegment(sketch, "E0.0.823", {"start": v(-221.41, 247.3) * mm, "end": v(-220.72, 246.78) * mm});
            skLineSegment(sketch, "E0.0.824", {"start": v(-220.72, 246.78) * mm, "end": v(-220.38, 246.51) * mm});
            skLineSegment(sketch, "E0.0.825", {"start": v(-220.38, 246.51) * mm, "end": v(-220.04, 246.25) * mm});
            skLineSegment(sketch, "E0.0.826", {"start": v(-220.04, 246.25) * mm, "end": v(-216.25, 248.8) * mm});
            skLineSegment(sketch, "E0.0.827", {"start": v(-216.25, 248.8) * mm, "end": v(-216.37, 249.2) * mm});
            skLineSegment(sketch, "E0.0.828", {"start": v(-216.37, 249.2) * mm, "end": v(-216.49, 249.63) * mm});
            skLineSegment(sketch, "E0.0.829", {"start": v(-216.49, 249.63) * mm, "end": v(-216.7, 250.46) * mm});
            skLineSegment(sketch, "E0.0.830", {"start": v(-216.7, 250.46) * mm, "end": v(-217.12, 252.16) * mm});
            skLineSegment(sketch, "E0.0.831", {"start": v(-217.12, 252.16) * mm, "end": v(-217.5, 253.89) * mm});
            skLineSegment(sketch, "E0.0.832", {"start": v(-217.5, 253.89) * mm, "end": v(-217.83, 255.63) * mm});
            skLineSegment(sketch, "E0.0.833", {"start": v(-217.83, 255.63) * mm, "end": v(-214.1, 257.96) * mm});
            skLineSegment(sketch, "E0.0.834", {"start": v(-214.1, 257.96) * mm, "end": v(-212.67, 256.9) * mm});
            skLineSegment(sketch, "E0.0.835", {"start": v(-212.67, 256.9) * mm, "end": v(-211.29, 255.8) * mm});
            skLineSegment(sketch, "E0.0.836", {"start": v(-211.29, 255.8) * mm, "end": v(-209.94, 254.68) * mm});
            skLineSegment(sketch, "E0.0.837", {"start": v(-209.94, 254.68) * mm, "end": v(-209.29, 254.1) * mm});
            skLineSegment(sketch, "E0.0.838", {"start": v(-209.29, 254.1) * mm, "end": v(-208.97, 253.82) * mm});
            skLineSegment(sketch, "E0.0.839", {"start": v(-208.97, 253.82) * mm, "end": v(-208.64, 253.53) * mm});
            skLineSegment(sketch, "E0.0.840", {"start": v(-208.64, 253.53) * mm, "end": v(-204.7, 255.8) * mm});
            skLineSegment(sketch, "E0.0.841", {"start": v(-204.7, 255.8) * mm, "end": v(-204.78, 256.23) * mm});
            skLineSegment(sketch, "E0.0.842", {"start": v(-204.78, 256.23) * mm, "end": v(-204.87, 256.65) * mm});
            skLineSegment(sketch, "E0.0.843", {"start": v(-204.87, 256.65) * mm, "end": v(-205.03, 257.5) * mm});
            skLineSegment(sketch, "E0.0.844", {"start": v(-205.03, 257.5) * mm, "end": v(-205.33, 259.23) * mm});
            skLineSegment(sketch, "E0.0.845", {"start": v(-205.33, 259.23) * mm, "end": v(-205.58, 260.97) * mm});
            skLineSegment(sketch, "E0.0.846", {"start": v(-205.58, 260.97) * mm, "end": v(-205.79, 262.74) * mm});
            skLineSegment(sketch, "E0.0.847", {"start": v(-205.79, 262.74) * mm, "end": v(-201.9, 264.8) * mm});
            skLineSegment(sketch, "E0.0.848", {"start": v(-201.9, 264.8) * mm, "end": v(-200.55, 263.64) * mm});
            skLineSegment(sketch, "E0.0.849", {"start": v(-200.55, 263.64) * mm, "end": v(-199.25, 262.45) * mm});
            skLineSegment(sketch, "E0.0.850", {"start": v(-199.25, 262.45) * mm, "end": v(-198, 261.24) * mm});
            skLineSegment(sketch, "E0.0.851", {"start": v(-198, 261.24) * mm, "end": v(-197.38, 260.62) * mm});
            skLineSegment(sketch, "E0.0.852", {"start": v(-197.38, 260.62) * mm, "end": v(-197.07, 260.31) * mm});
            skLineSegment(sketch, "E0.0.853", {"start": v(-197.07, 260.31) * mm, "end": v(-196.77, 260) * mm});
            skLineSegment(sketch, "E0.0.854", {"start": v(-196.77, 260) * mm, "end": v(-192.67, 262) * mm});
            skLineSegment(sketch, "E0.0.855", {"start": v(-192.67, 262) * mm, "end": v(-192.73, 262.42) * mm});
            skLineSegment(sketch, "E0.0.856", {"start": v(-192.73, 262.42) * mm, "end": v(-192.79, 262.85) * mm});
            skLineSegment(sketch, "E0.0.857", {"start": v(-192.79, 262.85) * mm, "end": v(-192.9, 263.71) * mm});
            skLineSegment(sketch, "E0.0.858", {"start": v(-192.9, 263.71) * mm, "end": v(-193.07, 265.45) * mm});
            skLineSegment(sketch, "E0.0.859", {"start": v(-193.07, 265.45) * mm, "end": v(-193.2, 267.21) * mm});
            skLineSegment(sketch, "E0.0.860", {"start": v(-193.2, 267.21) * mm, "end": v(-193.28, 268.99) * mm});
            skLineSegment(sketch, "E0.0.861", {"start": v(-193.28, 268.99) * mm, "end": v(-189.26, 270.77) * mm});
            skLineSegment(sketch, "E0.0.862", {"start": v(-189.26, 270.77) * mm, "end": v(-188, 269.52) * mm});
            skLineSegment(sketch, "E0.0.863", {"start": v(-188, 269.52) * mm, "end": v(-186.78, 268.24) * mm});
            skLineSegment(sketch, "E0.0.864", {"start": v(-186.78, 268.24) * mm, "end": v(-185.6, 266.95) * mm});
            skLineSegment(sketch, "E0.0.865", {"start": v(-185.6, 266.95) * mm, "end": v(-185.04, 266.3) * mm});
            skLineSegment(sketch, "E0.0.866", {"start": v(-185.04, 266.3) * mm, "end": v(-184.76, 265.96) * mm});
            skLineSegment(sketch, "E0.0.867", {"start": v(-184.76, 265.96) * mm, "end": v(-184.48, 265.63) * mm});
            skLineSegment(sketch, "E0.0.868", {"start": v(-184.48, 265.63) * mm, "end": v(-180.25, 267.33) * mm});
            skLineSegment(sketch, "E0.0.869", {"start": v(-180.25, 267.33) * mm, "end": v(-180.28, 267.76) * mm});
            skLineSegment(sketch, "E0.0.870", {"start": v(-180.28, 267.76) * mm, "end": v(-180.3, 268.2) * mm});
            skLineSegment(sketch, "E0.0.871", {"start": v(-180.3, 268.2) * mm, "end": v(-180.35, 269.06) * mm});
            skLineSegment(sketch, "E0.0.872", {"start": v(-180.35, 269.06) * mm, "end": v(-180.4, 270.8) * mm});
            skLineSegment(sketch, "E0.0.873", {"start": v(-180.4, 270.8) * mm, "end": v(-180.4, 272.57) * mm});
            skLineSegment(sketch, "E0.0.874", {"start": v(-180.4, 272.57) * mm, "end": v(-180.37, 274.35) * mm});
            skLineSegment(sketch, "E0.0.875", {"start": v(-180.37, 274.35) * mm, "end": v(-176.23, 275.85) * mm});
            skLineSegment(sketch, "E0.0.876", {"start": v(-176.23, 275.85) * mm, "end": v(-175.06, 274.5) * mm});
            skLineSegment(sketch, "E0.0.877", {"start": v(-175.06, 274.5) * mm, "end": v(-173.94, 273.15) * mm});
            skLineSegment(sketch, "E0.0.878", {"start": v(-173.94, 273.15) * mm, "end": v(-172.86, 271.78) * mm});
            skLineSegment(sketch, "E0.0.879", {"start": v(-172.86, 271.78) * mm, "end": v(-172.33, 271.08) * mm});
            skLineSegment(sketch, "E0.0.880", {"start": v(-172.33, 271.08) * mm, "end": v(-172.08, 270.73) * mm});
            skLineSegment(sketch, "E0.0.881", {"start": v(-172.08, 270.73) * mm, "end": v(-171.82, 270.39) * mm});
            skLineSegment(sketch, "E0.0.882", {"start": v(-171.82, 270.39) * mm, "end": v(-167.49, 271.79) * mm});
            skLineSegment(sketch, "E0.0.883", {"start": v(-167.49, 271.79) * mm, "end": v(-167.49, 272.22) * mm});
            skLineSegment(sketch, "E0.0.884", {"start": v(-167.49, 272.22) * mm, "end": v(-167.48, 272.65) * mm});
            skLineSegment(sketch, "E0.0.885", {"start": v(-167.48, 272.65) * mm, "end": v(-167.46, 273.52) * mm});
            skLineSegment(sketch, "E0.0.886", {"start": v(-167.46, 273.52) * mm, "end": v(-167.4, 275.27) * mm});
            skLineSegment(sketch, "E0.0.887", {"start": v(-167.4, 275.27) * mm, "end": v(-167.28, 277.03) * mm});
            skLineSegment(sketch, "E0.0.888", {"start": v(-167.28, 277.03) * mm, "end": v(-167.12, 278.8) * mm});
            skLineSegment(sketch, "E0.0.889", {"start": v(-167.12, 278.8) * mm, "end": v(-162.88, 280) * mm});
            skLineSegment(sketch, "E0.0.890", {"start": v(-162.88, 280) * mm, "end": v(-161.8, 278.59) * mm});
            skLineSegment(sketch, "E0.0.891", {"start": v(-161.8, 278.59) * mm, "end": v(-160.78, 277.15) * mm});
            skLineSegment(sketch, "E0.0.892", {"start": v(-160.78, 277.15) * mm, "end": v(-159.8, 275.7) * mm});
            skLineSegment(sketch, "E0.0.893", {"start": v(-159.8, 275.7) * mm, "end": v(-159.33, 274.98) * mm});
            skLineSegment(sketch, "E0.0.894", {"start": v(-159.33, 274.98) * mm, "end": v(-159.1, 274.61) * mm});
            skLineSegment(sketch, "E0.0.895", {"start": v(-159.1, 274.61) * mm, "end": v(-158.87, 274.25) * mm});
            skLineSegment(sketch, "E0.0.896", {"start": v(-158.87, 274.25) * mm, "end": v(-154.44, 275.34) * mm});
            skLineSegment(sketch, "E0.0.897", {"start": v(-154.44, 275.34) * mm, "end": v(-154.41, 275.77) * mm});
            skLineSegment(sketch, "E0.0.898", {"start": v(-154.41, 275.77) * mm, "end": v(-154.38, 276.2) * mm});
            skLineSegment(sketch, "E0.0.899", {"start": v(-154.38, 276.2) * mm, "end": v(-154.3, 277.07) * mm});
            skLineSegment(sketch, "E0.0.900", {"start": v(-154.3, 277.07) * mm, "end": v(-154.1, 278.8) * mm});
            skLineSegment(sketch, "E0.0.901", {"start": v(-154.1, 278.8) * mm, "end": v(-153.87, 280.55) * mm});
            skLineSegment(sketch, "E0.0.902", {"start": v(-153.87, 280.55) * mm, "end": v(-153.58, 282.3) * mm});
            skLineSegment(sketch, "E0.0.903", {"start": v(-153.58, 282.3) * mm, "end": v(-149.27, 283.22) * mm});
            skLineSegment(sketch, "E0.0.904", {"start": v(-149.27, 283.22) * mm, "end": v(-148.3, 281.73) * mm});
            skLineSegment(sketch, "E0.0.905", {"start": v(-148.3, 281.73) * mm, "end": v(-147.38, 280.23) * mm});
            skLineSegment(sketch, "E0.0.906", {"start": v(-147.38, 280.23) * mm, "end": v(-146.5, 278.72) * mm});
            skLineSegment(sketch, "E0.0.907", {"start": v(-146.5, 278.72) * mm, "end": v(-146.08, 277.96) * mm});
            skLineSegment(sketch, "E0.0.908", {"start": v(-146.08, 277.96) * mm, "end": v(-145.87, 277.58) * mm});
            skLineSegment(sketch, "E0.0.909", {"start": v(-145.87, 277.58) * mm, "end": v(-145.67, 277.2) * mm});
            skLineSegment(sketch, "E0.0.910", {"start": v(-145.67, 277.2) * mm, "end": v(-141.18, 277.98) * mm});
            skLineSegment(sketch, "E0.0.911", {"start": v(-141.18, 277.98) * mm, "end": v(-141.12, 278.4) * mm});
            skLineSegment(sketch, "E0.0.912", {"start": v(-141.12, 278.4) * mm, "end": v(-141.06, 278.84) * mm});
            skLineSegment(sketch, "E0.0.913", {"start": v(-141.06, 278.84) * mm, "end": v(-140.92, 279.7) * mm});
            skLineSegment(sketch, "E0.0.914", {"start": v(-140.92, 279.7) * mm, "end": v(-140.6, 281.41) * mm});
            skLineSegment(sketch, "E0.0.915", {"start": v(-140.6, 281.41) * mm, "end": v(-140.25, 283.14) * mm});
            skLineSegment(sketch, "E0.0.916", {"start": v(-140.25, 283.14) * mm, "end": v(-139.84, 284.87) * mm});
            skLineSegment(sketch, "E0.0.917", {"start": v(-139.84, 284.87) * mm, "end": v(-135.48, 285.48) * mm});
            skLineSegment(sketch, "E0.0.918", {"start": v(-135.48, 285.48) * mm, "end": v(-134.61, 283.92) * mm});
            skLineSegment(sketch, "E0.0.919", {"start": v(-134.61, 283.92) * mm, "end": v(-133.8, 282.36) * mm});
            skLineSegment(sketch, "E0.0.920", {"start": v(-133.8, 282.36) * mm, "end": v(-133.02, 280.8) * mm});
            skLineSegment(sketch, "E0.0.921", {"start": v(-133.02, 280.8) * mm, "end": v(-132.66, 280) * mm});
            skLineSegment(sketch, "E0.0.922", {"start": v(-132.66, 280) * mm, "end": v(-132.48, 279.6) * mm});
            skLineSegment(sketch, "E0.0.923", {"start": v(-132.48, 279.6) * mm, "end": v(-132.3, 279.21) * mm});
            skLineSegment(sketch, "E0.0.924", {"start": v(-132.3, 279.21) * mm, "end": v(-127.77, 279.68) * mm});
            skLineSegment(sketch, "E0.0.925", {"start": v(-127.77, 279.68) * mm, "end": v(-127.68, 280.1) * mm});
            skLineSegment(sketch, "E0.0.926", {"start": v(-127.68, 280.1) * mm, "end": v(-127.59, 280.53) * mm});
            skLineSegment(sketch, "E0.0.927", {"start": v(-127.59, 280.53) * mm, "end": v(-127.39, 281.38) * mm});
            skLineSegment(sketch, "E0.0.928", {"start": v(-127.39, 281.38) * mm, "end": v(-126.96, 283.07) * mm});
            skLineSegment(sketch, "E0.0.929", {"start": v(-126.96, 283.07) * mm, "end": v(-126.48, 284.77) * mm});
            skLineSegment(sketch, "E0.0.930", {"start": v(-126.48, 284.77) * mm, "end": v(-125.95, 286.46) * mm});
            skLineSegment(sketch, "E0.0.931", {"start": v(-125.95, 286.46) * mm, "end": v(-121.56, 286.76) * mm});
            skLineSegment(sketch, "E0.0.932", {"start": v(-121.56, 286.76) * mm, "end": v(-120.8, 285.15) * mm});
            skLineSegment(sketch, "E0.0.933", {"start": v(-120.8, 285.15) * mm, "end": v(-120.1, 283.54) * mm});
            skLineSegment(sketch, "E0.0.934", {"start": v(-120.1, 283.54) * mm, "end": v(-119.44, 281.92) * mm});
            skLineSegment(sketch, "E0.0.935", {"start": v(-119.44, 281.92) * mm, "end": v(-119.13, 281.1) * mm});
            skLineSegment(sketch, "E0.0.936", {"start": v(-119.13, 281.1) * mm, "end": v(-118.97, 280.7) * mm});
            skLineSegment(sketch, "E0.0.937", {"start": v(-118.97, 280.7) * mm, "end": v(-118.83, 280.3) * mm});
            skLineSegment(sketch, "E0.0.938", {"start": v(-118.83, 280.3) * mm, "end": v(-114.27, 280.45) * mm});
            skLineSegment(sketch, "E0.0.939", {"start": v(-114.27, 280.45) * mm, "end": v(-114.15, 280.87) * mm});
            skLineSegment(sketch, "E0.0.940", {"start": v(-114.15, 280.87) * mm, "end": v(-114.03, 281.28) * mm});
            skLineSegment(sketch, "E0.0.941", {"start": v(-114.03, 281.28) * mm, "end": v(-113.77, 282.11) * mm});
            skLineSegment(sketch, "E0.0.942", {"start": v(-113.77, 282.11) * mm, "end": v(-113.22, 283.77) * mm});
            skLineSegment(sketch, "E0.0.943", {"start": v(-113.22, 283.77) * mm, "end": v(-112.63, 285.43) * mm});
            skLineSegment(sketch, "E0.0.944", {"start": v(-112.63, 285.43) * mm, "end": v(-111.98, 287.09) * mm});
            skLineSegment(sketch, "E0.0.945", {"start": v(-111.98, 287.09) * mm, "end": v(-107.58, 287.08) * mm});
            skLineSegment(sketch, "E0.0.946", {"start": v(-107.58, 287.08) * mm, "end": v(-106.94, 285.42) * mm});
            skLineSegment(sketch, "E0.0.947", {"start": v(-106.94, 285.42) * mm, "end": v(-106.35, 283.76) * mm});
            skLineSegment(sketch, "E0.0.948", {"start": v(-106.35, 283.76) * mm, "end": v(-105.8, 282.1) * mm});
            skLineSegment(sketch, "E0.0.949", {"start": v(-105.8, 282.1) * mm, "end": v(-105.55, 281.27) * mm});
            skLineSegment(sketch, "E0.0.950", {"start": v(-105.55, 281.27) * mm, "end": v(-105.43, 280.85) * mm});
            skLineSegment(sketch, "E0.0.951", {"start": v(-105.43, 280.85) * mm, "end": v(-105.3, 280.44) * mm});
            skLineSegment(sketch, "E0.0.952", {"start": v(-105.3, 280.44) * mm, "end": v(-100.75, 280.27) * mm});
            skLineSegment(sketch, "E0.0.953", {"start": v(-100.75, 280.27) * mm, "end": v(-100.6, 280.68) * mm});
            skLineSegment(sketch, "E0.0.954", {"start": v(-100.6, 280.68) * mm, "end": v(-100.45, 281.08) * mm});
            skLineSegment(sketch, "E0.0.955", {"start": v(-100.45, 281.08) * mm, "end": v(-100.14, 281.9) * mm});
            skLineSegment(sketch, "E0.0.956", {"start": v(-100.14, 281.9) * mm, "end": v(-99.48, 283.51) * mm});
            skLineSegment(sketch, "E0.0.957", {"start": v(-99.48, 283.51) * mm, "end": v(-98.76, 285.12) * mm});
            skLineSegment(sketch, "E0.0.958", {"start": v(-98.76, 285.12) * mm, "end": v(-98, 286.73) * mm});
            skLineSegment(sketch, "E0.0.959", {"start": v(-98, 286.73) * mm, "end": v(-93.61, 286.42) * mm});
            skLineSegment(sketch, "E0.0.960", {"start": v(-93.61, 286.42) * mm, "end": v(-93.1, 284.72) * mm});
            skLineSegment(sketch, "E0.0.961", {"start": v(-93.1, 284.72) * mm, "end": v(-92.62, 283.02) * mm});
            skLineSegment(sketch, "E0.0.962", {"start": v(-92.62, 283.02) * mm, "end": v(-92.19, 281.33) * mm});
            skLineSegment(sketch, "E0.0.963", {"start": v(-92.19, 281.33) * mm, "end": v(-92, 280.48) * mm});
            skLineSegment(sketch, "E0.0.964", {"start": v(-92, 280.48) * mm, "end": v(-91.9, 280.06) * mm});
            skLineSegment(sketch, "E0.0.965", {"start": v(-91.9, 280.06) * mm, "end": v(-91.81, 279.63) * mm});
            skLineSegment(sketch, "E0.0.966", {"start": v(-91.81, 279.63) * mm, "end": v(-87.28, 279.15) * mm});
            skLineSegment(sketch, "E0.0.967", {"start": v(-87.28, 279.15) * mm, "end": v(-87.1, 279.55) * mm});
            skLineSegment(sketch, "E0.0.968", {"start": v(-87.1, 279.55) * mm, "end": v(-86.92, 279.94) * mm});
            skLineSegment(sketch, "E0.0.969", {"start": v(-86.92, 279.94) * mm, "end": v(-86.55, 280.73) * mm});
            skLineSegment(sketch, "E0.0.970", {"start": v(-86.55, 280.73) * mm, "end": v(-85.78, 282.3) * mm});
            skLineSegment(sketch, "E0.0.971", {"start": v(-85.78, 282.3) * mm, "end": v(-84.96, 283.85) * mm});
            skLineSegment(sketch, "E0.0.972", {"start": v(-84.96, 283.85) * mm, "end": v(-84.09, 285.4) * mm});
            skLineSegment(sketch, "E0.0.973", {"start": v(-84.09, 285.4) * mm, "end": v(-79.73, 284.79) * mm});
            skLineSegment(sketch, "E0.0.974", {"start": v(-79.73, 284.79) * mm, "end": v(-79.33, 283.05) * mm});
            skLineSegment(sketch, "E0.0.975", {"start": v(-79.33, 283.05) * mm, "end": v(-78.97, 281.33) * mm});
            skLineSegment(sketch, "E0.0.976", {"start": v(-78.97, 281.33) * mm, "end": v(-78.66, 279.6) * mm});
            skLineSegment(sketch, "E0.0.977", {"start": v(-78.66, 279.6) * mm, "end": v(-78.53, 278.75) * mm});
            skLineSegment(sketch, "E0.0.978", {"start": v(-78.53, 278.75) * mm, "end": v(-78.46, 278.32) * mm});
            skLineSegment(sketch, "E0.0.979", {"start": v(-78.46, 278.32) * mm, "end": v(-78.4, 277.9) * mm});
            skLineSegment(sketch, "E0.0.980", {"start": v(-78.4, 277.9) * mm, "end": v(-73.92, 277.1) * mm});
            skLineSegment(sketch, "E0.0.981", {"start": v(-73.92, 277.1) * mm, "end": v(-73.71, 277.48) * mm});
            skLineSegment(sketch, "E0.0.982", {"start": v(-73.71, 277.48) * mm, "end": v(-73.5, 277.86) * mm});
            skLineSegment(sketch, "E0.0.983", {"start": v(-73.5, 277.86) * mm, "end": v(-73.08, 278.61) * mm});
            skLineSegment(sketch, "E0.0.984", {"start": v(-73.08, 278.61) * mm, "end": v(-72.2, 280.12) * mm});
            skLineSegment(sketch, "E0.0.985", {"start": v(-72.2, 280.12) * mm, "end": v(-71.27, 281.62) * mm});
            skLineSegment(sketch, "E0.0.986", {"start": v(-71.27, 281.62) * mm, "end": v(-70.3, 283.1) * mm});
            skLineSegment(sketch, "E0.0.987", {"start": v(-70.3, 283.1) * mm, "end": v(-66, 282.19) * mm});
            skLineSegment(sketch, "E0.0.988", {"start": v(-66, 282.19) * mm, "end": v(-65.71, 280.43) * mm});
            skLineSegment(sketch, "E0.0.989", {"start": v(-65.71, 280.43) * mm, "end": v(-65.48, 278.68) * mm});
            skLineSegment(sketch, "E0.0.990", {"start": v(-65.48, 278.68) * mm, "end": v(-65.29, 276.95) * mm});
            skLineSegment(sketch, "E0.0.991", {"start": v(-65.29, 276.95) * mm, "end": v(-65.21, 276.08) * mm});
            skLineSegment(sketch, "E0.0.992", {"start": v(-65.21, 276.08) * mm, "end": v(-65.18, 275.65) * mm});
            skLineSegment(sketch, "E0.0.993", {"start": v(-65.18, 275.65) * mm, "end": v(-65.15, 275.22) * mm});
            skLineSegment(sketch, "E0.0.994", {"start": v(-65.15, 275.22) * mm, "end": v(-60.73, 274.1) * mm});
            skLineSegment(sketch, "E0.0.995", {"start": v(-60.73, 274.1) * mm, "end": v(-60.5, 274.48) * mm});
            skLineSegment(sketch, "E0.0.996", {"start": v(-60.5, 274.48) * mm, "end": v(-60.27, 274.84) * mm});
            skLineSegment(sketch, "E0.0.997", {"start": v(-60.27, 274.84) * mm, "end": v(-59.8, 275.57) * mm});
            skLineSegment(sketch, "E0.0.998", {"start": v(-59.8, 275.57) * mm, "end": v(-58.8, 277.01) * mm});
            skLineSegment(sketch, "E0.0.999", {"start": v(-58.8, 277.01) * mm, "end": v(-57.78, 278.44) * mm});
            skLineSegment(sketch, "E0.0.1000", {"start": v(-57.78, 278.44) * mm, "end": v(-56.7, 279.86) * mm});
            skLineSegment(sketch, "E0.0.1001", {"start": v(-56.7, 279.86) * mm, "end": v(-52.47, 278.64) * mm});
            skLineSegment(sketch, "E0.0.1002", {"start": v(-52.47, 278.64) * mm, "end": v(-52.31, 276.87) * mm});
            skLineSegment(sketch, "E0.0.1003", {"start": v(-52.31, 276.87) * mm, "end": v(-52.2, 275.1) * mm});
            skLineSegment(sketch, "E0.0.1004", {"start": v(-52.2, 275.1) * mm, "end": v(-52.13, 273.36) * mm});
            skLineSegment(sketch, "E0.0.1005", {"start": v(-52.13, 273.36) * mm, "end": v(-52.12, 272.5) * mm});
            skLineSegment(sketch, "E0.0.1006", {"start": v(-52.12, 272.5) * mm, "end": v(-52.12, 272.06) * mm});
            skLineSegment(sketch, "E0.0.1007", {"start": v(-52.12, 272.06) * mm, "end": v(-52.12, 271.63) * mm});
            skLineSegment(sketch, "E0.0.1008", {"start": v(-52.12, 271.63) * mm, "end": v(-47.78, 270.21) * mm});
            skLineSegment(sketch, "E0.0.1009", {"start": v(-47.78, 270.21) * mm, "end": v(-47.53, 270.56) * mm});
            skLineSegment(sketch, "E0.0.1010", {"start": v(-47.53, 270.56) * mm, "end": v(-47.27, 270.9) * mm});
            skLineSegment(sketch, "E0.0.1011", {"start": v(-47.27, 270.9) * mm, "end": v(-46.75, 271.6) * mm});
            skLineSegment(sketch, "E0.0.1012", {"start": v(-46.75, 271.6) * mm, "end": v(-45.66, 272.97) * mm});
            skLineSegment(sketch, "E0.0.1013", {"start": v(-45.66, 272.97) * mm, "end": v(-44.53, 274.33) * mm});
            skLineSegment(sketch, "E0.0.1014", {"start": v(-44.53, 274.33) * mm, "end": v(-43.36, 275.66) * mm});
            skLineSegment(sketch, "E0.0.1015", {"start": v(-43.36, 275.66) * mm, "end": v(-39.23, 274.15) * mm});
            skLineSegment(sketch, "E0.0.1016", {"start": v(-39.23, 274.15) * mm, "end": v(-39.2, 272.37) * mm});
            skLineSegment(sketch, "E0.0.1017", {"start": v(-39.2, 272.37) * mm, "end": v(-39.2, 270.61) * mm});
            skLineSegment(sketch, "E0.0.1018", {"start": v(-39.2, 270.61) * mm, "end": v(-39.26, 268.86) * mm});
            skLineSegment(sketch, "E0.0.1019", {"start": v(-39.26, 268.86) * mm, "end": v(-39.3, 268) * mm});
            skLineSegment(sketch, "E0.0.1020", {"start": v(-39.3, 268) * mm, "end": v(-39.33, 267.57) * mm});
            skLineSegment(sketch, "E0.0.1021", {"start": v(-39.33, 267.57) * mm, "end": v(-39.37, 267.13) * mm});
            skLineSegment(sketch, "E0.0.1022", {"start": v(-39.37, 267.13) * mm, "end": v(-35.14, 265.42) * mm});
            skLineSegment(sketch, "E0.0.1023", {"start": v(-35.14, 265.42) * mm, "end": v(-34.86, 265.75) * mm});
            skLineSegment(sketch, "E0.0.1024", {"start": v(-34.86, 265.75) * mm, "end": v(-34.58, 266.08) * mm});
            skLineSegment(sketch, "E0.0.1025", {"start": v(-34.58, 266.08) * mm, "end": v(-34, 266.73) * mm});
            skLineSegment(sketch, "E0.0.1026", {"start": v(-34, 266.73) * mm, "end": v(-32.83, 268.03) * mm});
            skLineSegment(sketch, "E0.0.1027", {"start": v(-32.83, 268.03) * mm, "end": v(-31.61, 269.3) * mm});
            skLineSegment(sketch, "E0.0.1028", {"start": v(-31.61, 269.3) * mm, "end": v(-30.35, 270.55) * mm});
            skLineSegment(sketch, "E0.0.1029", {"start": v(-30.35, 270.55) * mm, "end": v(-26.33, 268.75) * mm});
            skLineSegment(sketch, "E0.0.1030", {"start": v(-26.33, 268.75) * mm, "end": v(-26.42, 266.98) * mm});
            skLineSegment(sketch, "E0.0.1031", {"start": v(-26.42, 266.98) * mm, "end": v(-26.56, 265.22) * mm});
            skLineSegment(sketch, "E0.0.1032", {"start": v(-26.56, 265.22) * mm, "end": v(-26.73, 263.48) * mm});
            skLineSegment(sketch, "E0.0.1033", {"start": v(-26.73, 263.48) * mm, "end": v(-26.84, 262.62) * mm});
            skLineSegment(sketch, "E0.0.1034", {"start": v(-26.84, 262.62) * mm, "end": v(-26.9, 262.2) * mm});
            skLineSegment(sketch, "E0.0.1035", {"start": v(-26.9, 262.2) * mm, "end": v(-26.96, 261.76) * mm});
            skLineSegment(sketch, "E0.0.1036", {"start": v(-26.96, 261.76) * mm, "end": v(-22.86, 259.76) * mm});
            skLineSegment(sketch, "E0.0.1037", {"start": v(-22.86, 259.76) * mm, "end": v(-22.56, 260.07) * mm});
            skLineSegment(sketch, "E0.0.1038", {"start": v(-22.56, 260.07) * mm, "end": v(-22.26, 260.38) * mm});
            skLineSegment(sketch, "E0.0.1039", {"start": v(-22.26, 260.38) * mm, "end": v(-21.64, 261) * mm});
            skLineSegment(sketch, "E0.0.1040", {"start": v(-21.64, 261) * mm, "end": v(-20.38, 262.2) * mm});
            skLineSegment(sketch, "E0.0.1041", {"start": v(-20.38, 262.2) * mm, "end": v(-19.07, 263.38) * mm});
            skLineSegment(sketch, "E0.0.1042", {"start": v(-19.07, 263.38) * mm, "end": v(-17.73, 264.54) * mm});
            skLineSegment(sketch, "E0.0.1043", {"start": v(-17.73, 264.54) * mm, "end": v(-13.84, 262.47) * mm});
            skLineSegment(sketch, "E0.0.1044", {"start": v(-13.84, 262.47) * mm, "end": v(-14.06, 260.7) * mm});
            skLineSegment(sketch, "E0.0.1045", {"start": v(-14.06, 260.7) * mm, "end": v(-14.31, 258.96) * mm});
            skLineSegment(sketch, "E0.0.1046", {"start": v(-14.31, 258.96) * mm, "end": v(-14.61, 257.24) * mm});
            skLineSegment(sketch, "E0.0.1047", {"start": v(-14.61, 257.24) * mm, "end": v(-14.78, 256.39) * mm});
            skLineSegment(sketch, "E0.0.1048", {"start": v(-14.78, 256.39) * mm, "end": v(-14.86, 255.96) * mm});
            skLineSegment(sketch, "E0.0.1049", {"start": v(-14.86, 255.96) * mm, "end": v(-14.95, 255.54) * mm});
            skLineSegment(sketch, "E0.0.1050", {"start": v(-14.95, 255.54) * mm, "end": v(-11, 253.26) * mm});
            skLineSegment(sketch, "E0.0.1051", {"start": v(-11, 253.26) * mm, "end": v(-10.69, 253.54) * mm});
            skLineSegment(sketch, "E0.0.1052", {"start": v(-10.69, 253.54) * mm, "end": v(-10.36, 253.83) * mm});
            skLineSegment(sketch, "E0.0.1053", {"start": v(-10.36, 253.83) * mm, "end": v(-9.7, 254.4) * mm});
            skLineSegment(sketch, "E0.0.1054", {"start": v(-9.7, 254.4) * mm, "end": v(-8.36, 255.52) * mm});
            skLineSegment(sketch, "E0.0.1055", {"start": v(-8.36, 255.52) * mm, "end": v(-6.98, 256.6) * mm});
            skLineSegment(sketch, "E0.0.1056", {"start": v(-6.98, 256.6) * mm, "end": v(-5.55, 257.67) * mm});
            skLineSegment(sketch, "E0.0.1057", {"start": v(-5.55, 257.67) * mm, "end": v(-1.82, 255.33) * mm});
            skLineSegment(sketch, "E0.0.1058", {"start": v(-1.82, 255.33) * mm, "end": v(-2.16, 253.59) * mm});
            skLineSegment(sketch, "E0.0.1059", {"start": v(-2.16, 253.59) * mm, "end": v(-2.54, 251.86) * mm});
            skLineSegment(sketch, "E0.0.1060", {"start": v(-2.54, 251.86) * mm, "end": v(-2.95, 250.17) * mm});
            skLineSegment(sketch, "E0.0.1061", {"start": v(-2.95, 250.17) * mm, "end": v(-3.18, 249.33) * mm});
            skLineSegment(sketch, "E0.0.1062", {"start": v(-3.18, 249.33) * mm, "end": v(-3.3, 248.91) * mm});
            skLineSegment(sketch, "E0.0.1063", {"start": v(-3.3, 248.91) * mm, "end": v(-3.42, 248.5) * mm});
            skLineSegment(sketch, "E0.0.1064", {"start": v(-3.42, 248.5) * mm, "end": v(0.36, 245.94) * mm});
            skLineSegment(sketch, "E0.0.1065", {"start": v(0.36, 245.94) * mm, "end": v(0.7, 246.2) * mm});
            skLineSegment(sketch, "E0.0.1066", {"start": v(0.7, 246.2) * mm, "end": v(1.04, 246.47) * mm});
            skLineSegment(sketch, "E0.0.1067", {"start": v(1.04, 246.47) * mm, "end": v(1.74, 247) * mm});
            skLineSegment(sketch, "E0.0.1068", {"start": v(1.74, 247) * mm, "end": v(3.16, 248.01) * mm});
            skLineSegment(sketch, "E0.0.1069", {"start": v(3.16, 248.01) * mm, "end": v(4.62, 249) * mm});
            skLineSegment(sketch, "E0.0.1070", {"start": v(4.62, 249) * mm, "end": v(6.11, 249.96) * mm});
            skLineSegment(sketch, "E0.0.1071", {"start": v(6.11, 249.96) * mm, "end": v(9.67, 247.37) * mm});
            skLineSegment(sketch, "E0.0.1072", {"start": v(9.67, 247.37) * mm, "end": v(9.21, 245.65) * mm});
            skLineSegment(sketch, "E0.0.1073", {"start": v(9.21, 245.65) * mm, "end": v(8.72, 243.96) * mm});
            skLineSegment(sketch, "E0.0.1074", {"start": v(8.72, 243.96) * mm, "end": v(8.18, 242.3) * mm});
            skLineSegment(sketch, "E0.0.1075", {"start": v(8.18, 242.3) * mm, "end": v(7.9, 241.48) * mm});
            skLineSegment(sketch, "E0.0.1076", {"start": v(7.9, 241.48) * mm, "end": v(7.75, 241.07) * mm});
            skLineSegment(sketch, "E0.0.1077", {"start": v(7.75, 241.07) * mm, "end": v(7.6, 240.66) * mm});
            skLineSegment(sketch, "E0.0.1078", {"start": v(7.6, 240.66) * mm, "end": v(11.2, 237.85) * mm});
            skLineSegment(sketch, "E0.0.1079", {"start": v(11.2, 237.85) * mm, "end": v(11.55, 238.1) * mm});
            skLineSegment(sketch, "E0.0.1080", {"start": v(11.55, 238.1) * mm, "end": v(11.91, 238.33) * mm});
            skLineSegment(sketch, "E0.0.1081", {"start": v(11.91, 238.33) * mm, "end": v(12.64, 238.8) * mm});
            skLineSegment(sketch, "E0.0.1082", {"start": v(12.64, 238.8) * mm, "end": v(14.13, 239.72) * mm});
            skLineSegment(sketch, "E0.0.1083", {"start": v(14.13, 239.72) * mm, "end": v(15.65, 240.6) * mm});
            skLineSegment(sketch, "E0.0.1084", {"start": v(15.65, 240.6) * mm, "end": v(17.21, 241.46) * mm});
            skLineSegment(sketch, "E0.0.1085", {"start": v(17.21, 241.46) * mm, "end": v(20.58, 238.63) * mm});
            skLineSegment(sketch, "E0.0.1086", {"start": v(20.58, 238.63) * mm, "end": v(20, 236.95) * mm});
            skLineSegment(sketch, "E0.0.1087", {"start": v(20, 236.95) * mm, "end": v(19.4, 235.3) * mm});
            skLineSegment(sketch, "E0.0.1088", {"start": v(19.4, 235.3) * mm, "end": v(18.74, 233.67) * mm});
            skLineSegment(sketch, "E0.0.1089", {"start": v(18.74, 233.67) * mm, "end": v(18.4, 232.87) * mm});
            skLineSegment(sketch, "E0.0.1090", {"start": v(18.4, 232.87) * mm, "end": v(18.23, 232.47) * mm});
            skLineSegment(sketch, "E0.0.1091", {"start": v(18.23, 232.47) * mm, "end": v(18.05, 232.08) * mm});
            skLineSegment(sketch, "E0.0.1092", {"start": v(18.05, 232.08) * mm, "end": v(21.43, 229.02) * mm});
            skLineSegment(sketch, "E0.0.1093", {"start": v(21.43, 229.02) * mm, "end": v(21.8, 229.24) * mm});
            skLineSegment(sketch, "E0.0.1094", {"start": v(21.8, 229.24) * mm, "end": v(22.19, 229.45) * mm});
            skLineSegment(sketch, "E0.0.1095", {"start": v(22.19, 229.45) * mm, "end": v(22.95, 229.87) * mm});
            skLineSegment(sketch, "E0.0.1096", {"start": v(22.95, 229.87) * mm, "end": v(24.5, 230.68) * mm});
            skLineSegment(sketch, "E0.0.1097", {"start": v(24.5, 230.68) * mm, "end": v(26.08, 231.46) * mm});
            skLineSegment(sketch, "E0.0.1098", {"start": v(26.08, 231.46) * mm, "end": v(27.7, 232.2) * mm});
            skLineSegment(sketch, "E0.0.1099", {"start": v(27.7, 232.2) * mm, "end": v(30.85, 229.14) * mm});
            skLineSegment(sketch, "E0.0.1100", {"start": v(30.85, 229.14) * mm, "end": v(30.16, 227.5) * mm});
            skLineSegment(sketch, "E0.0.1101", {"start": v(30.16, 227.5) * mm, "end": v(29.43, 225.9) * mm});
            skLineSegment(sketch, "E0.0.1102", {"start": v(29.43, 225.9) * mm, "end": v(28.67, 224.33) * mm});
            skLineSegment(sketch, "E0.0.1103", {"start": v(28.67, 224.33) * mm, "end": v(28.28, 223.55) * mm});
            skLineSegment(sketch, "E0.0.1104", {"start": v(28.28, 223.55) * mm, "end": v(28.08, 223.17) * mm});
            skLineSegment(sketch, "E0.0.1105", {"start": v(28.08, 223.17) * mm, "end": v(27.87, 222.79) * mm});
            skLineSegment(sketch, "E0.0.1106", {"start": v(27.87, 222.79) * mm, "end": v(31.04, 219.5) * mm});
            skLineSegment(sketch, "E0.0.1107", {"start": v(31.04, 219.5) * mm, "end": v(31.42, 219.7) * mm});
            skLineSegment(sketch, "E0.0.1108", {"start": v(31.42, 219.7) * mm, "end": v(31.82, 219.88) * mm});
            skLineSegment(sketch, "E0.0.1109", {"start": v(31.82, 219.88) * mm, "end": v(32.6, 220.25) * mm});
            skLineSegment(sketch, "E0.0.1110", {"start": v(32.6, 220.25) * mm, "end": v(34.2, 220.95) * mm});
            skLineSegment(sketch, "E0.0.1111", {"start": v(34.2, 220.95) * mm, "end": v(35.84, 221.61) * mm});
            skLineSegment(sketch, "E0.0.1112", {"start": v(35.84, 221.61) * mm, "end": v(37.5, 222.24) * mm});
            skLineSegment(sketch, "E0.0.1113", {"start": v(37.5, 222.24) * mm, "end": v(40.44, 218.97) * mm});
            skLineSegment(sketch, "E0.0.1114", {"start": v(40.44, 218.97) * mm, "end": v(39.64, 217.38) * mm});
            skLineSegment(sketch, "E0.0.1115", {"start": v(39.64, 217.38) * mm, "end": v(38.8, 215.83) * mm});
            skLineSegment(sketch, "E0.0.1116", {"start": v(38.8, 215.83) * mm, "end": v(37.93, 214.32) * mm});
            skLineSegment(sketch, "E0.0.1117", {"start": v(37.93, 214.32) * mm, "end": v(37.48, 213.57) * mm});
            skLineSegment(sketch, "E0.0.1118", {"start": v(37.48, 213.57) * mm, "end": v(37.25, 213.2) * mm});
            skLineSegment(sketch, "E0.0.1119", {"start": v(37.25, 213.2) * mm, "end": v(37.02, 212.84) * mm});
            skLineSegment(sketch, "E0.0.1120", {"start": v(37.02, 212.84) * mm, "end": v(39.95, 209.34) * mm});
            skLineSegment(sketch, "E0.0.1121", {"start": v(39.95, 209.34) * mm, "end": v(40.35, 209.5) * mm});
            skLineSegment(sketch, "E0.0.1122", {"start": v(40.35, 209.5) * mm, "end": v(40.75, 209.66) * mm});
            skLineSegment(sketch, "E0.0.1123", {"start": v(40.75, 209.66) * mm, "end": v(41.56, 209.97) * mm});
            skLineSegment(sketch, "E0.0.1124", {"start": v(41.56, 209.97) * mm, "end": v(43.21, 210.56) * mm});
            skLineSegment(sketch, "E0.0.1125", {"start": v(43.21, 210.56) * mm, "end": v(44.89, 211.1) * mm});
            skLineSegment(sketch, "E0.0.1126", {"start": v(44.89, 211.1) * mm, "end": v(46.59, 211.62) * mm});
            skLineSegment(sketch, "E0.0.1127", {"start": v(46.59, 211.62) * mm, "end": v(49.3, 208.15) * mm});
            skLineSegment(sketch, "E0.0.1128", {"start": v(49.3, 208.15) * mm, "end": v(48.38, 206.62) * mm});
            skLineSegment(sketch, "E0.0.1129", {"start": v(48.38, 206.62) * mm, "end": v(47.44, 205.13) * mm});
            skLineSegment(sketch, "E0.0.1130", {"start": v(47.44, 205.13) * mm, "end": v(46.46, 203.68) * mm});
            skLineSegment(sketch, "E0.0.1131", {"start": v(46.46, 203.68) * mm, "end": v(45.96, 202.97) * mm});
            skLineSegment(sketch, "E0.0.1132", {"start": v(45.96, 202.97) * mm, "end": v(45.71, 202.62) * mm});
            skLineSegment(sketch, "E0.0.1133", {"start": v(45.71, 202.62) * mm, "end": v(45.46, 202.27) * mm});
            skLineSegment(sketch, "E0.0.1134", {"start": v(45.46, 202.27) * mm, "end": v(48.13, 198.58) * mm});
            skLineSegment(sketch, "E0.0.1135", {"start": v(48.13, 198.58) * mm, "end": v(48.54, 198.71) * mm});
            skLineSegment(sketch, "E0.0.1136", {"start": v(48.54, 198.71) * mm, "end": v(48.96, 198.84) * mm});
            skLineSegment(sketch, "E0.0.1137", {"start": v(48.96, 198.84) * mm, "end": v(49.79, 199.1) * mm});
            skLineSegment(sketch, "E0.0.1138", {"start": v(49.79, 199.1) * mm, "end": v(51.47, 199.56) * mm});
            skLineSegment(sketch, "E0.0.1139", {"start": v(51.47, 199.56) * mm, "end": v(53.18, 200) * mm});
            skLineSegment(sketch, "E0.0.1140", {"start": v(53.18, 200) * mm, "end": v(54.91, 200.39) * mm});
            skLineSegment(sketch, "E0.0.1141", {"start": v(54.91, 200.39) * mm, "end": v(57.37, 196.74) * mm});
            skLineSegment(sketch, "E0.0.1142", {"start": v(57.37, 196.74) * mm, "end": v(56.35, 195.28) * mm});
            skLineSegment(sketch, "E0.0.1143", {"start": v(56.35, 195.28) * mm, "end": v(55.3, 193.86) * mm});
            skLineSegment(sketch, "E0.0.1144", {"start": v(55.3, 193.86) * mm, "end": v(54.24, 192.48) * mm});
            skLineSegment(sketch, "E0.0.1145", {"start": v(54.24, 192.48) * mm, "end": v(53.69, 191.8) * mm});
            skLineSegment(sketch, "E0.0.1146", {"start": v(53.69, 191.8) * mm, "end": v(53.41, 191.47) * mm});
            skLineSegment(sketch, "E0.0.1147", {"start": v(53.41, 191.47) * mm, "end": v(53.13, 191.14) * mm});
            skLineSegment(sketch, "E0.0.1148", {"start": v(53.13, 191.14) * mm, "end": v(55.54, 187.27) * mm});
            skLineSegment(sketch, "E0.0.1149", {"start": v(55.54, 187.27) * mm, "end": v(55.96, 187.37) * mm});
            skLineSegment(sketch, "E0.0.1150", {"start": v(55.96, 187.37) * mm, "end": v(56.38, 187.47) * mm});
            skLineSegment(sketch, "E0.0.1151", {"start": v(56.38, 187.47) * mm, "end": v(57.23, 187.67) * mm});
            skLineSegment(sketch, "E0.0.1152", {"start": v(57.23, 187.67) * mm, "end": v(58.94, 188.02) * mm});
            skLineSegment(sketch, "E0.0.1153", {"start": v(58.94, 188.02) * mm, "end": v(60.68, 188.33) * mm});
            skLineSegment(sketch, "E0.0.1154", {"start": v(60.68, 188.33) * mm, "end": v(62.44, 188.6) * mm});
            skLineSegment(sketch, "E0.0.1155", {"start": v(62.44, 188.6) * mm, "end": v(64.63, 184.79) * mm});
            skLineSegment(sketch, "E0.0.1156", {"start": v(64.63, 184.79) * mm, "end": v(63.51, 183.4) * mm});
            skLineSegment(sketch, "E0.0.1157", {"start": v(63.51, 183.4) * mm, "end": v(62.37, 182.06) * mm});
            skLineSegment(sketch, "E0.0.1158", {"start": v(62.37, 182.06) * mm, "end": v(61.2, 180.76) * mm});
            skLineSegment(sketch, "E0.0.1159", {"start": v(61.2, 180.76) * mm, "end": v(60.61, 180.13) * mm});
            skLineSegment(sketch, "E0.0.1160", {"start": v(60.61, 180.13) * mm, "end": v(60.32, 179.81) * mm});
            skLineSegment(sketch, "E0.0.1161", {"start": v(60.32, 179.81) * mm, "end": v(60.02, 179.5) * mm});
            skLineSegment(sketch, "E0.0.1162", {"start": v(60.02, 179.5) * mm, "end": v(62.15, 175.47) * mm});
            skLineSegment(sketch, "E0.0.1163", {"start": v(62.15, 175.47) * mm, "end": v(62.58, 175.55) * mm});
            skLineSegment(sketch, "E0.0.1164", {"start": v(62.58, 175.55) * mm, "end": v(63, 175.62) * mm});
            skLineSegment(sketch, "E0.0.1165", {"start": v(63, 175.62) * mm, "end": v(63.86, 175.75) * mm});
            skLineSegment(sketch, "E0.0.1166", {"start": v(63.86, 175.75) * mm, "end": v(65.6, 175.99) * mm});
            skLineSegment(sketch, "E0.0.1167", {"start": v(65.6, 175.99) * mm, "end": v(67.35, 176.18) * mm});
            skLineSegment(sketch, "E0.0.1168", {"start": v(67.35, 176.18) * mm, "end": v(69.12, 176.32) * mm});
            skLineSegment(sketch, "E0.0.1169", {"start": v(69.12, 176.32) * mm, "end": v(71.04, 172.36) * mm});
            skLineSegment(sketch, "E0.0.1170", {"start": v(71.04, 172.36) * mm, "end": v(69.83, 171.06) * mm});
            skLineSegment(sketch, "E0.0.1171", {"start": v(69.83, 171.06) * mm, "end": v(68.6, 169.8) * mm});
            skLineSegment(sketch, "E0.0.1172", {"start": v(68.6, 169.8) * mm, "end": v(67.34, 168.58) * mm});
            skLineSegment(sketch, "E0.0.1173", {"start": v(67.34, 168.58) * mm, "end": v(66.7, 168) * mm});
            skLineSegment(sketch, "E0.0.1174", {"start": v(66.7, 168) * mm, "end": v(66.39, 167.7) * mm});
            skLineSegment(sketch, "E0.0.1175", {"start": v(66.39, 167.7) * mm, "end": v(66.07, 167.41) * mm});
            skLineSegment(sketch, "E0.0.1176", {"start": v(66.07, 167.41) * mm, "end": v(67.92, 163.24) * mm});
            skLineSegment(sketch, "E0.0.1177", {"start": v(67.92, 163.24) * mm, "end": v(68.35, 163.29) * mm});
            skLineSegment(sketch, "E0.0.1178", {"start": v(68.35, 163.29) * mm, "end": v(68.78, 163.33) * mm});
            skLineSegment(sketch, "E0.0.1179", {"start": v(68.78, 163.33) * mm, "end": v(69.64, 163.4) * mm});
            skLineSegment(sketch, "E0.0.1180", {"start": v(69.64, 163.4) * mm, "end": v(71.39, 163.52) * mm});
            skLineSegment(sketch, "E0.0.1181", {"start": v(71.39, 163.52) * mm, "end": v(73.15, 163.58) * mm});
            skLineSegment(sketch, "E0.0.1182", {"start": v(73.15, 163.58) * mm, "end": v(74.93, 163.6) * mm});
            skLineSegment(sketch, "E0.0.1183", {"start": v(74.93, 163.6) * mm, "end": v(76.57, 159.52) * mm});
            skLineSegment(sketch, "E0.0.1184", {"start": v(76.57, 159.52) * mm, "end": v(75.27, 158.3) * mm});
            skLineSegment(sketch, "E0.0.1185", {"start": v(75.27, 158.3) * mm, "end": v(73.95, 157.14) * mm});
            skLineSegment(sketch, "E0.0.1186", {"start": v(73.95, 157.14) * mm, "end": v(72.62, 156) * mm});
            skLineSegment(sketch, "E0.0.1187", {"start": v(72.62, 156) * mm, "end": v(71.94, 155.46) * mm});
            skLineSegment(sketch, "E0.0.1188", {"start": v(71.94, 155.46) * mm, "end": v(71.6, 155.2) * mm});
            skLineSegment(sketch, "E0.0.1189", {"start": v(71.6, 155.2) * mm, "end": v(71.26, 154.93) * mm});
            skLineSegment(sketch, "E0.0.1190", {"start": v(71.26, 154.93) * mm, "end": v(72.82, 150.64) * mm});
            skLineSegment(sketch, "E0.0.1191", {"start": v(72.82, 150.64) * mm, "end": v(73.25, 150.66) * mm});
            skLineSegment(sketch, "E0.0.1192", {"start": v(73.25, 150.66) * mm, "end": v(73.68, 150.67) * mm});
            skLineSegment(sketch, "E0.0.1193", {"start": v(73.68, 150.67) * mm, "end": v(74.55, 150.68) * mm});
            skLineSegment(sketch, "E0.0.1194", {"start": v(74.55, 150.68) * mm, "end": v(76.3, 150.67) * mm});
            skLineSegment(sketch, "E0.0.1195", {"start": v(76.3, 150.67) * mm, "end": v(78.06, 150.62) * mm});
            skLineSegment(sketch, "E0.0.1196", {"start": v(78.06, 150.62) * mm, "end": v(79.83, 150.52) * mm});
            skLineSegment(sketch, "E0.0.1197", {"start": v(79.83, 150.52) * mm, "end": v(81.19, 146.33) * mm});
            skLineSegment(sketch, "E0.0.1198", {"start": v(81.19, 146.33) * mm, "end": v(79.8, 145.2) * mm});
            skLineSegment(sketch, "E0.0.1199", {"start": v(79.8, 145.2) * mm, "end": v(78.41, 144.13) * mm});
            skLineSegment(sketch, "E0.0.1200", {"start": v(78.41, 144.13) * mm, "end": v(77, 143.1) * mm});
            skLineSegment(sketch, "E0.0.1201", {"start": v(77, 143.1) * mm, "end": v(76.29, 142.6) * mm});
            skLineSegment(sketch, "E0.0.1202", {"start": v(76.29, 142.6) * mm, "end": v(75.93, 142.36) * mm});
            skLineSegment(sketch, "E0.0.1203", {"start": v(75.93, 142.36) * mm, "end": v(75.57, 142.11) * mm});
            skLineSegment(sketch, "E0.0.1204", {"start": v(75.57, 142.11) * mm, "end": v(76.82, 137.73) * mm});
            skLineSegment(sketch, "E0.0.1205", {"start": v(76.82, 137.73) * mm, "end": v(77.26, 137.72) * mm});
            skLineSegment(sketch, "E0.0.1206", {"start": v(77.26, 137.72) * mm, "end": v(77.69, 137.7) * mm});
            skLineSegment(sketch, "E0.0.1207", {"start": v(77.69, 137.7) * mm, "end": v(78.56, 137.65) * mm});
            skLineSegment(sketch, "E0.0.1208", {"start": v(78.56, 137.65) * mm, "end": v(80.3, 137.52) * mm});
            skLineSegment(sketch, "E0.0.1209", {"start": v(80.3, 137.52) * mm, "end": v(82.05, 137.34) * mm});
            skLineSegment(sketch, "E0.0.1210", {"start": v(82.05, 137.34) * mm, "end": v(83.82, 137.12) * mm});
            skLineSegment(sketch, "E0.0.1211", {"start": v(83.82, 137.12) * mm, "end": v(84.87, 132.84) * mm});
            skLineSegment(sketch, "E0.0.1212", {"start": v(84.87, 132.84) * mm, "end": v(83.42, 131.82) * mm});
            skLineSegment(sketch, "E0.0.1213", {"start": v(83.42, 131.82) * mm, "end": v(81.95, 130.84) * mm});
            skLineSegment(sketch, "E0.0.1214", {"start": v(81.95, 130.84) * mm, "end": v(80.47, 129.91) * mm});
            skLineSegment(sketch, "E0.0.1215", {"start": v(80.47, 129.91) * mm, "end": v(79.73, 129.47) * mm});
            skLineSegment(sketch, "E0.0.1216", {"start": v(79.73, 129.47) * mm, "end": v(79.35, 129.25) * mm});
            skLineSegment(sketch, "E0.0.1217", {"start": v(79.35, 129.25) * mm, "end": v(78.98, 129.03) * mm});
            skLineSegment(sketch, "E0.0.1218", {"start": v(78.98, 129.03) * mm, "end": v(79.92, 124.57) * mm});
            skLineSegment(sketch, "E0.0.1219", {"start": v(79.92, 124.57) * mm, "end": v(80.35, 124.52) * mm});
            skLineSegment(sketch, "E0.0.1220", {"start": v(80.35, 124.52) * mm, "end": v(80.78, 124.48) * mm});
            skLineSegment(sketch, "E0.0.1221", {"start": v(80.78, 124.48) * mm, "end": v(81.64, 124.37) * mm});
            skLineSegment(sketch, "E0.0.1222", {"start": v(81.64, 124.37) * mm, "end": v(83.37, 124.11) * mm});
            skLineSegment(sketch, "E0.0.1223", {"start": v(83.37, 124.11) * mm, "end": v(85.1, 123.81) * mm});
            skLineSegment(sketch, "E0.0.1224", {"start": v(85.1, 123.81) * mm, "end": v(86.85, 123.47) * mm});
            skLineSegment(sketch, "E0.0.1225", {"start": v(86.85, 123.47) * mm, "end": v(87.61, 119.13) * mm});
            skLineSegment(sketch, "E0.0.1226", {"start": v(87.61, 119.13) * mm, "end": v(86.09, 118.21) * mm});
            skLineSegment(sketch, "E0.0.1227", {"start": v(86.09, 118.21) * mm, "end": v(84.56, 117.34) * mm});
            skLineSegment(sketch, "E0.0.1228", {"start": v(84.56, 117.34) * mm, "end": v(83.02, 116.52) * mm});
            skLineSegment(sketch, "E0.0.1229", {"start": v(83.02, 116.52) * mm, "end": v(82.24, 116.12) * mm});
            skLineSegment(sketch, "E0.0.1230", {"start": v(82.24, 116.12) * mm, "end": v(81.85, 115.93) * mm});
            skLineSegment(sketch, "E0.0.1231", {"start": v(81.85, 115.93) * mm, "end": v(81.47, 115.74) * mm});
            skLineSegment(sketch, "E0.0.1232", {"start": v(81.47, 115.74) * mm, "end": v(82.1, 111.23) * mm});
            skLineSegment(sketch, "E0.0.1233", {"start": v(82.1, 111.23) * mm, "end": v(82.52, 111.15) * mm});
            skLineSegment(sketch, "E0.0.1234", {"start": v(82.52, 111.15) * mm, "end": v(82.94, 111.07) * mm});
            skLineSegment(sketch, "E0.0.1235", {"start": v(82.94, 111.07) * mm, "end": v(83.8, 110.9) * mm});
            skLineSegment(sketch, "E0.0.1236", {"start": v(83.8, 110.9) * mm, "end": v(85.5, 110.53) * mm});
            skLineSegment(sketch, "E0.0.1237", {"start": v(85.5, 110.53) * mm, "end": v(87.22, 110.1) * mm});
            skLineSegment(sketch, "E0.0.1238", {"start": v(87.22, 110.1) * mm, "end": v(88.93, 109.64) * mm});
            skLineSegment(sketch, "E0.0.1239", {"start": v(88.93, 109.64) * mm, "end": v(89.39, 105.26) * mm});
            skLineSegment(sketch, "E0.0.1240", {"start": v(89.39, 105.26) * mm, "end": v(87.8, 104.45) * mm});
            skLineSegment(sketch, "E0.0.1241", {"start": v(87.8, 104.45) * mm, "end": v(86.21, 103.7) * mm});
            skLineSegment(sketch, "E0.0.1242", {"start": v(86.21, 103.7) * mm, "end": v(84.62, 102.98) * mm});
            skLineSegment(sketch, "E0.0.1243", {"start": v(84.62, 102.98) * mm, "end": v(83.82, 102.64) * mm});
            skLineSegment(sketch, "E0.0.1244", {"start": v(83.82, 102.64) * mm, "end": v(83.42, 102.47) * mm});
            skLineSegment(sketch, "E0.0.1245", {"start": v(83.42, 102.47) * mm, "end": v(83.02, 102.31) * mm});
            skLineSegment(sketch, "E0.0.1246", {"start": v(83.02, 102.31) * mm, "end": v(83.33, 97.76) * mm});
            skLineSegment(sketch, "E0.0.1247", {"start": v(83.33, 97.76) * mm, "end": v(83.75, 97.66) * mm});
            skLineSegment(sketch, "E0.0.1248", {"start": v(83.75, 97.66) * mm, "end": v(84.17, 97.55) * mm});
            skLineSegment(sketch, "E0.0.1249", {"start": v(84.17, 97.55) * mm, "end": v(85, 97.32) * mm});
            skLineSegment(sketch, "E0.0.1250", {"start": v(85, 97.32) * mm, "end": v(86.68, 96.83) * mm});
            skLineSegment(sketch, "E0.0.1251", {"start": v(86.68, 96.83) * mm, "end": v(88.36, 96.3) * mm});
            skLineSegment(sketch, "E0.0.1252", {"start": v(88.36, 96.3) * mm, "end": v(90.04, 95.7) * mm});
            skLineSegment(sketch, "E0.0.1253", {"start": v(90.04, 95.7) * mm, "end": v(90.19, 91.3) * mm});
            skLineSegment(sketch, "E0.0.1254", {"start": v(90.19, 91.3) * mm, "end": v(88.55, 90.6) * mm});
            skLineSegment(sketch, "E0.0.1255", {"start": v(88.55, 90.6) * mm, "end": v(86.91, 89.96) * mm});
            skLineSegment(sketch, "E0.0.1256", {"start": v(86.91, 89.96) * mm, "end": v(85.27, 89.36) * mm});
            skLineSegment(sketch, "E0.0.1257", {"start": v(85.27, 89.36) * mm, "end": v(84.45, 89.07) * mm});
            skLineSegment(sketch, "E0.0.1258", {"start": v(84.45, 89.07) * mm, "end": v(84.04, 88.94) * mm});
            skLineSegment(sketch, "E0.0.1259", {"start": v(84.04, 88.94) * mm, "end": v(83.63, 88.8) * mm});
            skCircle(sketch, "E1", {"center": v(-110.06, 86.8) * mm, "radius": 5 * mm, "construction": true});
            skCircle(sketch, "E2", {"center": v(-110.06, 86.8) * mm, "radius": 125 * mm});
            skSolve(sketch);
        }
        {
            var Q0;
            Q0=makeQuery(id+"F0.imprint","IMPRINT",FACE,{"disambiguationData":[TD([[makeQuery(id+"F0.imprint","IMPRINT",EDGE,{"derivedFrom":sQuery(id+"F0.wireOp",EDGE,"E0.0.0")}),-1.0]])]});
            extrude(context, id + "F1", {"entities" : qUnion([Q0]), "depth" : 9 * mm, "offsetDistance" : 25 * mm});
        }
    });
